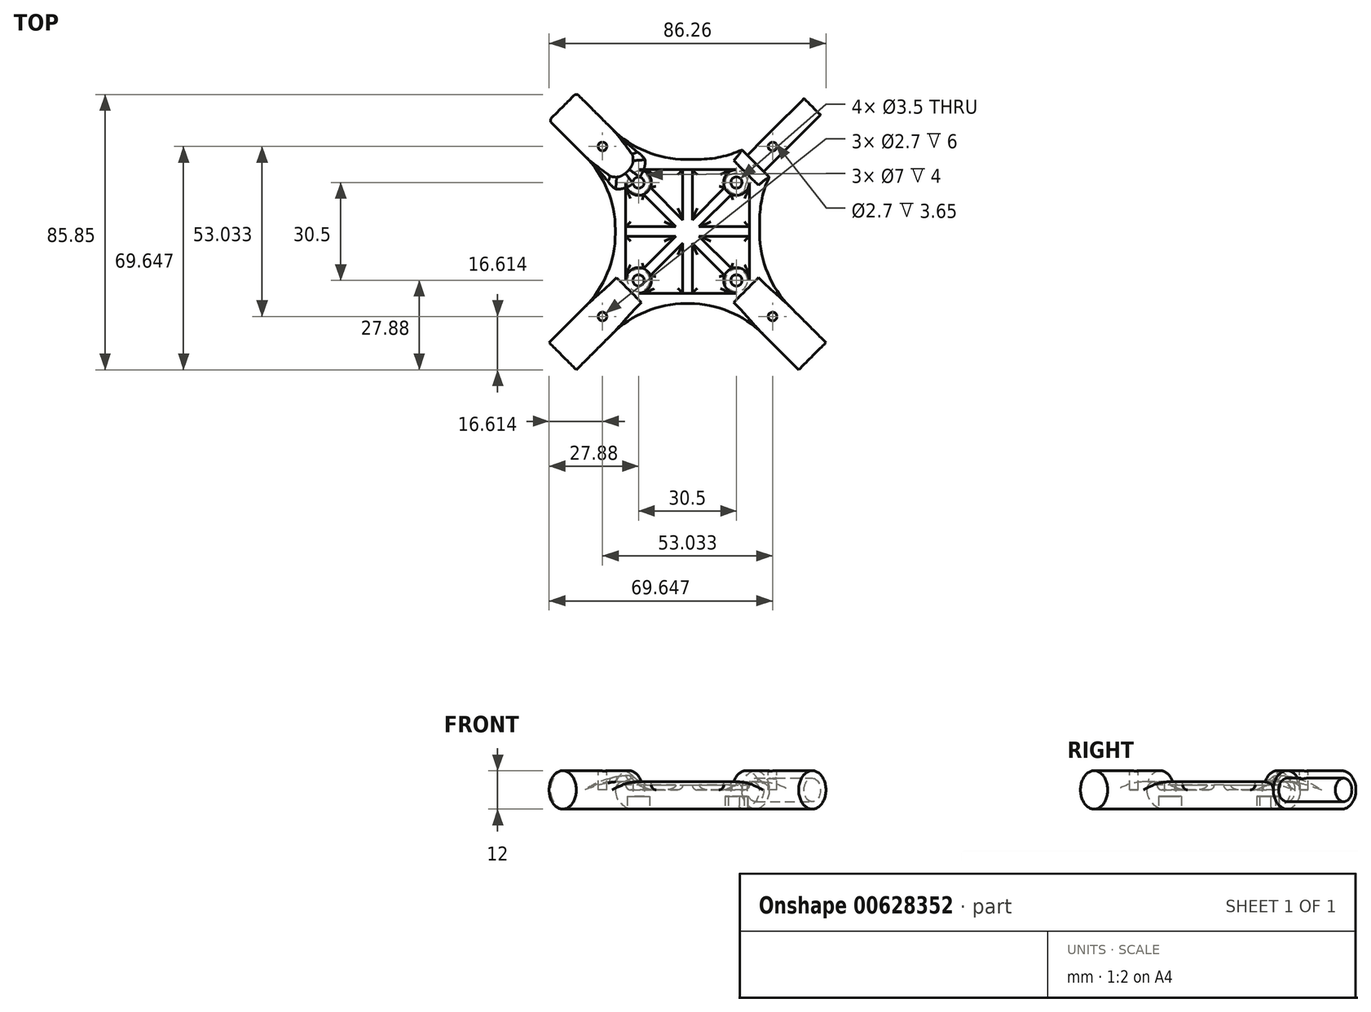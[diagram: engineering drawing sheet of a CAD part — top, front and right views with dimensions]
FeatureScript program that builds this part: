
annotation { "Feature Type Name" : "Feature", "Feature Type Description" : "" }
export const myFeature = defineFeature(function(context is Context, id is Id, definition is map)
    precondition{}
    {
        {
            var Q0;
            Q0=qCreatedBy(makeId("Top.planeOp"),FACE);
            var sketch = newSketch(context, id + "F0", { "sketchPlane" : qUnion([Q0])});
            skLineSegment(sketch, "E0.bottom", {"start": v(15.25, 15.25) * mm, "end": v(-15.25, 15.25) * mm});
            skLineSegment(sketch, "E0.top", {"start": v(15.25, -15.25) * mm, "end": v(-15.25, -15.25) * mm});
            skLineSegment(sketch, "E0.left", {"start": v(15.25, 15.25) * mm, "end": v(15.25, -15.25) * mm});
            skLineSegment(sketch, "E0.right", {"start": v(-15.25, 15.25) * mm, "end": v(-15.25, -15.25) * mm});
            skPoint(sketch, "E0.middle", {"position": v(0, 0) * mm});
            skCircle(sketch, "E1", {"center": v(-15.25, 15.25) * mm, "radius": 1.75 * mm});
            skCircle(sketch, "E2", {"center": v(15.25, 15.25) * mm, "radius": 1.75 * mm});
            skCircle(sketch, "E3", {"center": v(15.25, -15.25) * mm, "radius": 1.75 * mm});
            skCircle(sketch, "E4", {"center": v(-15.25, -15.25) * mm, "radius": 1.75 * mm});
            skLineSegment(sketch, "E5.bottom", {"start": v(22.5, 22.5) * mm, "end": v(-22.5, 22.5) * mm});
            skLineSegment(sketch, "E5.top", {"start": v(22.5, -22.5) * mm, "end": v(-22.5, -22.5) * mm});
            skLineSegment(sketch, "E5.left", {"start": v(22.5, 22.5) * mm, "end": v(22.5, -22.5) * mm});
            skLineSegment(sketch, "E5.right", {"start": v(-22.5, 22.5) * mm, "end": v(-22.5, -22.5) * mm});
            skSolve(sketch);
        }
        {
            var Q0;
            Q0=makeQuery(id+"F0.imprint","IMPRINT",FACE,{"disambiguationData":[TD([[makeQuery(id+"F0.imprint","IMPRINT",EDGE,{"derivedFrom":sQuery(id+"F0.wireOp",EDGE,"E5.bottom")}),1.0]])]});
            var Q1;
            {var subQ5=sQuery(id+"F0.wireOp",EDGE,"E2");var subQ13=sQuery(id+"F0.wireOp",EDGE,"E0.bottom");var subQ14=makeQuery(id+"F0.imprint","INTERSECT",VERTEX,{"derivedFrom":[subQ13,subQ5]});Q1=makeQuery(id+"F0.imprint","IMPRINT",FACE,{"disambiguationData":[TD([[makeQuery(id+"F0.imprint","IMPRINT",EDGE,{"disambiguationData":[TD([[subQ14,-1.0]])],"derivedFrom":subQ13}),1.0]])]});}
            extrude(context, id + "F1", {"entities" : qUnion([Q0, Q1]), "endBound" : BoundingType.SYMMETRIC, "depth" : 5 * mm, "offsetDistance" : 25 * mm});
        }
        {
            var Q0;
            Q0=makeQuery(id+"F1.opExtrude","CAP_FACE",FACE,{"disambiguationData":[OSD([sQuery(id+"F0.wireOp",EDGE,"E1"),sQuery(id+"F0.wireOp",EDGE,"E2"),sQuery(id+"F0.wireOp",EDGE,"E3"),sQuery(id+"F0.wireOp",EDGE,"E4"),sQuery(id+"F0.wireOp",EDGE,"E5.bottom"),sQuery(id+"F0.wireOp",EDGE,"E5.top"),sQuery(id+"F0.wireOp",EDGE,"E5.left"),sQuery(id+"F0.wireOp",EDGE,"E5.right")])],"isStart":false});
            var sketch = newSketch(context, id + "F2", { "sketchPlane" : qUnion([Q0])});
            skLineSegment(sketch, "E6", {"start": v(-22.5, 22.5) * mm, "end": v(0, 0) * mm});
            skLineSegment(sketch, "E7", {"start": v(0, 0) * mm, "end": v(22.5, 22.5) * mm});
            skLineSegment(sketch, "E8", {"start": v(22.5, -22.5) * mm, "end": v(0, 0) * mm});
            skLineSegment(sketch, "E9", {"start": v(-22.5, -22.5) * mm, "end": v(0, 0) * mm});
            skLineSegment(sketch, "E10", {"start": v(0, 0) * mm, "end": v(0, 22.5) * mm});
            skLineSegment(sketch, "E11", {"start": v(0, 0) * mm, "end": v(-22.5, 0) * mm});
            skLineSegment(sketch, "E12", {"start": v(0, 0) * mm, "end": v(22.5, 0) * mm});
            skLineSegment(sketch, "E13", {"start": v(0, 0) * mm, "end": v(0, -22.5) * mm});
            skCircle(sketch, "E14", {"center": v(-15.25, 15.25) * mm, "radius": 4 * mm});
            skCircle(sketch, "E15", {"center": v(15.25, 15.25) * mm, "radius": 4 * mm});
            skCircle(sketch, "E16", {"center": v(15.25, -15.25) * mm, "radius": 4 * mm});
            skCircle(sketch, "E17", {"center": v(-15.25, -15.25) * mm, "radius": 4 * mm});
            skLineSegment(sketch, "E18.0", {"start": v(15.25, 19.25) * mm, "end": v(-15.25, 19.25) * mm});
            skLineSegment(sketch, "E18.1", {"start": v(19.25, 15.25) * mm, "end": v(19.25, -15.25) * mm});
            skLineSegment(sketch, "E18.2", {"start": v(15.25, -19.25) * mm, "end": v(-15.25, -19.25) * mm});
            skLineSegment(sketch, "E18.3", {"start": v(-19.25, 15.25) * mm, "end": v(-19.25, -15.25) * mm});
            skLineSegment(sketch, "E19.0", {"start": v(1.5, 0) * mm, "end": v(1.5, 22.5) * mm});
            skLineSegment(sketch, "E19.1", {"start": v(1.5, 0) * mm, "end": v(1.5, -22.5) * mm});
            skLineSegment(sketch, "E20.0", {"start": v(-1.5, 0) * mm, "end": v(-1.5, 22.5) * mm});
            skLineSegment(sketch, "E20.1", {"start": v(-1.5, 0) * mm, "end": v(-1.5, -22.5) * mm});
            skLineSegment(sketch, "E21.0", {"start": v(0, 1.5) * mm, "end": v(-22.5, 1.5) * mm});
            skLineSegment(sketch, "E21.1", {"start": v(0, 1.5) * mm, "end": v(22.5, 1.5) * mm});
            skLineSegment(sketch, "E22.0", {"start": v(0, -1.5) * mm, "end": v(-22.5, -1.5) * mm});
            skLineSegment(sketch, "E22.1", {"start": v(0, -1.5) * mm, "end": v(22.5, -1.5) * mm});
            skLineSegment(sketch, "E23.0", {"start": v(21.44, -23.56) * mm, "end": v(-1.06, -1.06) * mm});
            skLineSegment(sketch, "E23.1", {"start": v(-23.56, 21.44) * mm, "end": v(-1.06, -1.06) * mm});
            skLineSegment(sketch, "E24.0", {"start": v(1.06, -1.06) * mm, "end": v(23.56, 21.44) * mm});
            skLineSegment(sketch, "E24.1", {"start": v(-21.44, -23.56) * mm, "end": v(1.06, -1.06) * mm});
            skLineSegment(sketch, "E25.0", {"start": v(-1.06, 1.06) * mm, "end": v(21.44, 23.56) * mm});
            skLineSegment(sketch, "E25.1", {"start": v(-23.56, -21.44) * mm, "end": v(-1.06, 1.06) * mm});
            skLineSegment(sketch, "E26.0", {"start": v(23.56, -21.44) * mm, "end": v(1.06, 1.06) * mm});
            skLineSegment(sketch, "E26.1", {"start": v(-21.44, 23.56) * mm, "end": v(1.06, 1.06) * mm});
            skSolve(sketch);
        }
        {
            var Q0;
            {var subQ0=sQuery(id+"F2.wireOp",EDGE,"E18.0");var subQ1=sQuery(id+"F2.wireOp",EDGE,"E15");var subQ2=makeQuery(id+"F2.imprint","INTERSECT",VERTEX,{"derivedFrom":[subQ1,subQ0]});Q0=makeQuery(id+"F2.imprint","IMPRINT",FACE,{"disambiguationData":[TD([[makeQuery(id+"F2.imprint","IMPRINT",EDGE,{"disambiguationData":[TD([[subQ2,-1.0]])],"derivedFrom":subQ1}),-1.0]])]});}
            var Q1;
            {var subQ0=sQuery(id+"F2.wireOp",EDGE,"E18.0");var subQ1=sQuery(id+"F2.wireOp",EDGE,"E14");var subQ2=makeQuery(id+"F2.imprint","INTERSECT",VERTEX,{"derivedFrom":[subQ1,subQ0]});Q1=makeQuery(id+"F2.imprint","IMPRINT",FACE,{"disambiguationData":[TD([[makeQuery(id+"F2.imprint","IMPRINT",EDGE,{"disambiguationData":[TD([[subQ2,1.0]])],"derivedFrom":subQ1}),-1.0]])]});}
            var Q2;
            {var subQ0=sQuery(id+"F2.wireOp",EDGE,"E18.3");var subQ1=sQuery(id+"F2.wireOp",EDGE,"E14");var subQ2=makeQuery(id+"F2.imprint","INTERSECT",VERTEX,{"derivedFrom":[subQ1,subQ0]});Q2=makeQuery(id+"F2.imprint","IMPRINT",FACE,{"disambiguationData":[TD([[makeQuery(id+"F2.imprint","IMPRINT",EDGE,{"disambiguationData":[TD([[subQ2,-1.0]])],"derivedFrom":subQ1}),-1.0]])]});}
            var Q3;
            {var subQ0=sQuery(id+"F2.wireOp",EDGE,"E18.3");var subQ1=sQuery(id+"F2.wireOp",EDGE,"E17");var subQ2=makeQuery(id+"F2.imprint","INTERSECT",VERTEX,{"derivedFrom":[subQ1,subQ0]});Q3=makeQuery(id+"F2.imprint","IMPRINT",FACE,{"disambiguationData":[TD([[makeQuery(id+"F2.imprint","IMPRINT",EDGE,{"disambiguationData":[TD([[subQ2,1.0]])],"derivedFrom":subQ1}),-1.0]])]});}
            var Q4;
            {var subQ0=sQuery(id+"F2.wireOp",EDGE,"E18.2");var subQ1=sQuery(id+"F2.wireOp",EDGE,"E17");var subQ2=makeQuery(id+"F2.imprint","INTERSECT",VERTEX,{"derivedFrom":[subQ1,subQ0]});Q4=makeQuery(id+"F2.imprint","IMPRINT",FACE,{"disambiguationData":[TD([[makeQuery(id+"F2.imprint","IMPRINT",EDGE,{"disambiguationData":[TD([[subQ2,-1.0]])],"derivedFrom":subQ1}),-1.0]])]});}
            var Q5;
            {var subQ0=sQuery(id+"F2.wireOp",EDGE,"E18.2");var subQ1=sQuery(id+"F2.wireOp",EDGE,"E16");var subQ2=makeQuery(id+"F2.imprint","INTERSECT",VERTEX,{"derivedFrom":[subQ1,subQ0]});Q5=makeQuery(id+"F2.imprint","IMPRINT",FACE,{"disambiguationData":[TD([[makeQuery(id+"F2.imprint","IMPRINT",EDGE,{"disambiguationData":[TD([[subQ2,1.0]])],"derivedFrom":subQ1}),-1.0]])]});}
            var Q6;
            {var subQ0=sQuery(id+"F2.wireOp",EDGE,"E18.1");var subQ1=sQuery(id+"F2.wireOp",EDGE,"E16");var subQ2=makeQuery(id+"F2.imprint","INTERSECT",VERTEX,{"derivedFrom":[subQ1,subQ0]});Q6=makeQuery(id+"F2.imprint","IMPRINT",FACE,{"disambiguationData":[TD([[makeQuery(id+"F2.imprint","IMPRINT",EDGE,{"disambiguationData":[TD([[subQ2,-1.0]])],"derivedFrom":subQ1}),-1.0]])]});}
            var Q7;
            {var subQ0=sQuery(id+"F2.wireOp",EDGE,"E18.1");var subQ1=sQuery(id+"F2.wireOp",EDGE,"E15");var subQ2=makeQuery(id+"F2.imprint","INTERSECT",VERTEX,{"derivedFrom":[subQ1,subQ0]});Q7=makeQuery(id+"F2.imprint","IMPRINT",FACE,{"disambiguationData":[TD([[makeQuery(id+"F2.imprint","IMPRINT",EDGE,{"disambiguationData":[TD([[subQ2,1.0]])],"derivedFrom":subQ1}),-1.0]])]});}
            extrude(context, id + "F3", {"entities" : qUnion([Q0, Q1, Q2, Q3, Q4, Q5, Q6, Q7]), "operationType" : NewBodyOperationType.REMOVE, "oppositeDirection" : true, "depth" : 2.5 * mm, "offsetDistance" : 25 * mm});
        }
        {
            var Q0;
            Q0=makeQuery(id+"F3.boolean.opBoolean","COPY",FACE,{"derivedFrom":makeQuery(id+"F3.opExtrude","CAP_FACE",FACE,{"disambiguationData":[OSD([sQuery(id+"F2.wireOp",EDGE,"E16"),sQuery(id+"F2.wireOp",EDGE,"E18.2"),sQuery(id+"F2.wireOp",EDGE,"E19.1"),sQuery(id+"F2.wireOp",EDGE,"E23.0")])],"isStart":false})});
            var Q1;
            Q1=makeQuery(id+"F3.boolean.opBoolean","COPY",FACE,{"derivedFrom":makeQuery(id+"F3.opExtrude","CAP_FACE",FACE,{"disambiguationData":[OSD([sQuery(id+"F2.wireOp",EDGE,"E17"),sQuery(id+"F2.wireOp",EDGE,"E18.2"),sQuery(id+"F2.wireOp",EDGE,"E20.1"),sQuery(id+"F2.wireOp",EDGE,"E24.1")])],"isStart":false})});
            var Q2;
            Q2=makeQuery(id+"F3.boolean.opBoolean","COPY",FACE,{"derivedFrom":makeQuery(id+"F3.opExtrude","CAP_FACE",FACE,{"disambiguationData":[OSD([sQuery(id+"F2.wireOp",EDGE,"E17"),sQuery(id+"F2.wireOp",EDGE,"E18.3"),sQuery(id+"F2.wireOp",EDGE,"E22.0"),sQuery(id+"F2.wireOp",EDGE,"E25.1")])],"isStart":false})});
            var Q3;
            Q3=makeQuery(id+"F3.boolean.opBoolean","COPY",FACE,{"derivedFrom":makeQuery(id+"F3.opExtrude","CAP_FACE",FACE,{"disambiguationData":[OSD([sQuery(id+"F2.wireOp",EDGE,"E14"),sQuery(id+"F2.wireOp",EDGE,"E18.3"),sQuery(id+"F2.wireOp",EDGE,"E21.0"),sQuery(id+"F2.wireOp",EDGE,"E23.1")])],"isStart":false})});
            var Q4;
            Q4=makeQuery(id+"F3.boolean.opBoolean","COPY",FACE,{"derivedFrom":makeQuery(id+"F3.opExtrude","CAP_FACE",FACE,{"disambiguationData":[OSD([sQuery(id+"F2.wireOp",EDGE,"E14"),sQuery(id+"F2.wireOp",EDGE,"E18.0"),sQuery(id+"F2.wireOp",EDGE,"E20.0"),sQuery(id+"F2.wireOp",EDGE,"E26.1")])],"isStart":false})});
            var Q5;
            Q5=makeQuery(id+"F3.boolean.opBoolean","COPY",FACE,{"derivedFrom":makeQuery(id+"F3.opExtrude","CAP_FACE",FACE,{"disambiguationData":[OSD([sQuery(id+"F2.wireOp",EDGE,"E15"),sQuery(id+"F2.wireOp",EDGE,"E18.0"),sQuery(id+"F2.wireOp",EDGE,"E19.0"),sQuery(id+"F2.wireOp",EDGE,"E25.0")])],"isStart":false})});
            var Q6;
            Q6=makeQuery(id+"F3.boolean.opBoolean","COPY",FACE,{"derivedFrom":makeQuery(id+"F3.opExtrude","CAP_FACE",FACE,{"disambiguationData":[OSD([sQuery(id+"F2.wireOp",EDGE,"E15"),sQuery(id+"F2.wireOp",EDGE,"E18.1"),sQuery(id+"F2.wireOp",EDGE,"E21.1"),sQuery(id+"F2.wireOp",EDGE,"E24.0")])],"isStart":false})});
            var Q7;
            Q7=makeQuery(id+"F3.boolean.opBoolean","COPY",FACE,{"derivedFrom":makeQuery(id+"F3.opExtrude","CAP_FACE",FACE,{"disambiguationData":[OSD([sQuery(id+"F2.wireOp",EDGE,"E16"),sQuery(id+"F2.wireOp",EDGE,"E18.1"),sQuery(id+"F2.wireOp",EDGE,"E22.1"),sQuery(id+"F2.wireOp",EDGE,"E26.0")])],"isStart":false})});
            fillet(context, id + "F4", {"entities" : qUnion([Q0, Q1, Q2, Q3, Q4, Q5, Q6, Q7]), "radius" : 1.5 * mm, "tangentPropagation" : true, "allowEdgeOverflow" : false});
        }
        {
            var Q0;
            Q0=qCreatedBy(makeId("Top.planeOp"),FACE);
            var sketch = newSketch(context, id + "F5", { "sketchPlane" : qUnion([Q0])});
            skLineSegment(sketch, "E27", {"start": v(0, 0) * mm, "end": v(-28.28, 28.28) * mm});
            skLineSegment(sketch, "E28", {"start": v(0, 0) * mm, "end": v(28.28, 28.28) * mm});
            skLineSegment(sketch, "E29", {"start": v(0, 0) * mm, "end": v(28.28, -28.28) * mm});
            skLineSegment(sketch, "E30", {"start": v(0, 0) * mm, "end": v(-28.28, -28.28) * mm});
            skLineSegment(sketch, "E31.0", {"start": v(4.24, -4.24) * mm, "end": v(32.53, 24.04) * mm});
            skLineSegment(sketch, "E31.1", {"start": v(4.24, -4.24) * mm, "end": v(-24.04, -32.53) * mm});
            skLineSegment(sketch, "E32.0", {"start": v(-4.24, 4.24) * mm, "end": v(-32.53, -24.04) * mm});
            skLineSegment(sketch, "E32.1", {"start": v(-4.24, 4.24) * mm, "end": v(24.04, 32.53) * mm});
            skLineSegment(sketch, "E33.0", {"start": v(-4.24, -4.24) * mm, "end": v(-32.53, 24.04) * mm});
            skLineSegment(sketch, "E33.1", {"start": v(-4.24, -4.24) * mm, "end": v(24.04, -32.53) * mm});
            skLineSegment(sketch, "E34.0", {"start": v(4.24, 4.24) * mm, "end": v(-24.04, 32.53) * mm});
            skLineSegment(sketch, "E34.1", {"start": v(4.24, 4.24) * mm, "end": v(32.53, -24.04) * mm});
            skLineSegment(sketch, "E35", {"start": v(24.04, -32.53) * mm, "end": v(32.53, -24.04) * mm});
            skLineSegment(sketch, "E36", {"start": v(-32.53, -24.04) * mm, "end": v(-24.04, -32.53) * mm});
            skLineSegment(sketch, "E37", {"start": v(24.04, 32.53) * mm, "end": v(32.53, 24.04) * mm});
            skLineSegment(sketch, "E38", {"start": v(-24.04, 32.53) * mm, "end": v(-32.53, 24.04) * mm});
            skLineSegment(sketch, "E39", {"start": v(22.5, 14.01) * mm, "end": v(14.01, 22.5) * mm});
            skLineSegment(sketch, "E40", {"start": v(22.5, -14.01) * mm, "end": v(14.01, -22.5) * mm});
            skLineSegment(sketch, "E41", {"start": v(-22.5, -14.01) * mm, "end": v(-14.01, -22.5) * mm});
            skLineSegment(sketch, "E42", {"start": v(-14.01, 22.5) * mm, "end": v(-22.5, 14.01) * mm});
            skSolve(sketch);
        }
        {
            var Q0;
            {var subQ0=sQuery(id+"F5.wireOp",EDGE,"E38");var subQ1=sQuery(id+"F5.wireOp",EDGE,"E27");var subQ2=makeQuery(id+"F5.imprint","INTERSECT",VERTEX,{"derivedFrom":[subQ1,subQ0]});Q0=makeQuery(id+"F5.imprint","IMPRINT",FACE,{"disambiguationData":[TD([[makeQuery(id+"F5.imprint","IMPRINT",EDGE,{"disambiguationData":[TD([[subQ2,1.0]])],"derivedFrom":subQ1}),-1.0]])]});}
            var Q1;
            {var subQ0=sQuery(id+"F5.wireOp",EDGE,"E38");var subQ1=sQuery(id+"F5.wireOp",EDGE,"E27");var subQ2=makeQuery(id+"F5.imprint","INTERSECT",VERTEX,{"derivedFrom":[subQ1,subQ0]});Q1=makeQuery(id+"F5.imprint","IMPRINT",FACE,{"disambiguationData":[TD([[makeQuery(id+"F5.imprint","IMPRINT",EDGE,{"disambiguationData":[TD([[subQ2,1.0]])],"derivedFrom":subQ1}),1.0]])]});}
            var Q2;
            {var subQ0=sQuery(id+"F5.wireOp",EDGE,"E36");var subQ1=sQuery(id+"F5.wireOp",EDGE,"E30");var subQ2=makeQuery(id+"F5.imprint","INTERSECT",VERTEX,{"derivedFrom":[subQ1,subQ0]});Q2=makeQuery(id+"F5.imprint","IMPRINT",FACE,{"disambiguationData":[TD([[makeQuery(id+"F5.imprint","IMPRINT",EDGE,{"disambiguationData":[TD([[subQ2,1.0]])],"derivedFrom":subQ1}),-1.0]])]});}
            var Q3;
            {var subQ0=sQuery(id+"F5.wireOp",EDGE,"E36");var subQ1=sQuery(id+"F5.wireOp",EDGE,"E30");var subQ2=makeQuery(id+"F5.imprint","INTERSECT",VERTEX,{"derivedFrom":[subQ1,subQ0]});Q3=makeQuery(id+"F5.imprint","IMPRINT",FACE,{"disambiguationData":[TD([[makeQuery(id+"F5.imprint","IMPRINT",EDGE,{"disambiguationData":[TD([[subQ2,1.0]])],"derivedFrom":subQ1}),1.0]])]});}
            var Q4;
            {var subQ0=sQuery(id+"F5.wireOp",EDGE,"E37");var subQ1=sQuery(id+"F5.wireOp",EDGE,"E28");var subQ2=makeQuery(id+"F5.imprint","INTERSECT",VERTEX,{"derivedFrom":[subQ1,subQ0]});Q4=makeQuery(id+"F5.imprint","IMPRINT",FACE,{"disambiguationData":[TD([[makeQuery(id+"F5.imprint","IMPRINT",EDGE,{"disambiguationData":[TD([[subQ2,1.0]])],"derivedFrom":subQ1}),1.0]])]});}
            var Q5;
            {var subQ0=sQuery(id+"F5.wireOp",EDGE,"E37");var subQ1=sQuery(id+"F5.wireOp",EDGE,"E28");var subQ2=makeQuery(id+"F5.imprint","INTERSECT",VERTEX,{"derivedFrom":[subQ1,subQ0]});Q5=makeQuery(id+"F5.imprint","IMPRINT",FACE,{"disambiguationData":[TD([[makeQuery(id+"F5.imprint","IMPRINT",EDGE,{"disambiguationData":[TD([[subQ2,1.0]])],"derivedFrom":subQ1}),-1.0]])]});}
            var Q6;
            {var subQ0=sQuery(id+"F5.wireOp",EDGE,"E35");var subQ1=sQuery(id+"F5.wireOp",EDGE,"E29");var subQ2=makeQuery(id+"F5.imprint","INTERSECT",VERTEX,{"derivedFrom":[subQ1,subQ0]});Q6=makeQuery(id+"F5.imprint","IMPRINT",FACE,{"disambiguationData":[TD([[makeQuery(id+"F5.imprint","IMPRINT",EDGE,{"disambiguationData":[TD([[subQ2,1.0]])],"derivedFrom":subQ1}),1.0]])]});}
            var Q7;
            {var subQ0=sQuery(id+"F5.wireOp",EDGE,"E35");var subQ1=sQuery(id+"F5.wireOp",EDGE,"E29");var subQ2=makeQuery(id+"F5.imprint","INTERSECT",VERTEX,{"derivedFrom":[subQ1,subQ0]});Q7=makeQuery(id+"F5.imprint","IMPRINT",FACE,{"disambiguationData":[TD([[makeQuery(id+"F5.imprint","IMPRINT",EDGE,{"disambiguationData":[TD([[subQ2,1.0]])],"derivedFrom":subQ1}),-1.0]])]});}
            extrude(context, id + "F6", {"entities" : qUnion([Q0, Q1, Q2, Q3, Q4, Q5, Q6, Q7]), "operationType" : NewBodyOperationType.ADD, "endBound" : BoundingType.SYMMETRIC, "depth" : 12 * mm, "offsetDistance" : 25 * mm});
        }
        {
            var Q0;
            Q0=makeQuery(id+"F6.opExtrude","SWEPT_FACE",FACE,{"disambiguationData":[OSD([sQuery(id+"F5.wireOp",EDGE,"E38")])]});
            extrude(context, id + "F7", {"entities" : qUnion([Q0]), "operationType" : NewBodyOperationType.ADD, "depth" : 15 * mm, "offsetDistance" : 25 * mm});
        }
        {
            var Q0;
            Q0=makeQuery(id+"F6.opExtrude","SWEPT_FACE",FACE,{"disambiguationData":[OSD([sQuery(id+"F5.wireOp",EDGE,"E36")])]});
            extrude(context, id + "F8", {"entities" : qUnion([Q0]), "operationType" : NewBodyOperationType.ADD, "depth" : 15 * mm, "offsetDistance" : 25 * mm});
        }
        {
            var Q0;
            Q0=makeQuery(id+"F6.opExtrude","SWEPT_FACE",FACE,{"disambiguationData":[OSD([sQuery(id+"F5.wireOp",EDGE,"E35")])]});
            extrude(context, id + "F9", {"entities" : qUnion([Q0]), "operationType" : NewBodyOperationType.ADD, "depth" : 15 * mm, "offsetDistance" : 25 * mm});
        }
        {
            var Q0;
            Q0=makeQuery(id+"F6.opExtrude","SWEPT_FACE",FACE,{"disambiguationData":[OSD([sQuery(id+"F5.wireOp",EDGE,"E37")])]});
            extrude(context, id + "F10", {"entities" : qUnion([Q0]), "operationType" : NewBodyOperationType.ADD, "depth" : 15 * mm, "offsetDistance" : 25 * mm});
        }
        {
            var Q0;
            Q0=makeQuery(id+"F10.opExtrude","CAP_FACE",FACE,{"disambiguationData":[OSD([sQuery(id+"F5.wireOp",EDGE,"E37")])],"isStart":false});
            var sketch = newSketch(context, id + "F11", { "sketchPlane" : qUnion([Q0])});
            skLineSegment(sketch, "E43", {"start": v(6, 6) * mm, "end": v(-6, -6) * mm});
            skCircle(sketch, "E44", {"center": v(0, 0) * mm, "radius": 3.65 * mm});
            skSolve(sketch);
        }
        {
            var Q0;
            {var subQ0=sQuery(id+"F11.wireOp",EDGE,"E44");var subQ1=sQuery(id+"F11.wireOp",EDGE,"E43");var subQ2=makeQuery(id+"F11.imprint","INTERSECT",VERTEX,{"disambiguationData":[OD(0.0)],"derivedFrom":[subQ1,subQ0]});Q0=makeQuery(id+"F11.imprint","IMPRINT",FACE,{"disambiguationData":[TD([[makeQuery(id+"F11.imprint","IMPRINT",EDGE,{"disambiguationData":[TD([[subQ2,-1.0]])],"derivedFrom":subQ1}),-1.0]])]});}
            var Q1;
            {var subQ0=sQuery(id+"F11.wireOp",EDGE,"E44");var subQ1=sQuery(id+"F11.wireOp",EDGE,"E43");var subQ2=makeQuery(id+"F11.imprint","INTERSECT",VERTEX,{"disambiguationData":[OD(0.0)],"derivedFrom":[subQ1,subQ0]});Q1=makeQuery(id+"F11.imprint","IMPRINT",FACE,{"disambiguationData":[TD([[makeQuery(id+"F11.imprint","IMPRINT",EDGE,{"disambiguationData":[TD([[subQ2,-1.0]])],"derivedFrom":subQ1}),1.0]])]});}
            extrude(context, id + "F12", {"entities" : qUnion([Q0, Q1]), "operationType" : NewBodyOperationType.REMOVE, "oppositeDirection" : true, "depth" : 25 * mm, "offsetDistance" : 25 * mm});
        }
        {
            var Q0;
            Q0=qCreatedBy(makeId("Right.planeOp"),FACE);
            var sketch = newSketch(context, id + "F13", { "sketchPlane" : qUnion([Q0])});
            skLineSegment(sketch, "E45", {"start": v(0, 0) * mm, "end": v(0, 67.2) * mm});
            skSolve(sketch);
        }
        {
            var Q0;
            {var subQ0=sQuery(id+"F5.wireOp",EDGE,"E37");Q0=makeQuery(id+"F10.boolean.opBoolean","MERGE",FACE,{"derivedFrom":[makeQuery(id+"F6.opExtrude","CAP_FACE",FACE,{"disambiguationData":[OSD([sQuery(id+"F5.wireOp",EDGE,"E31.0"),sQuery(id+"F5.wireOp",EDGE,"E32.1"),subQ0,sQuery(id+"F5.wireOp",EDGE,"E39")])],"isStart":false}),makeQuery(id+"F10.opExtrude","SWEPT_FACE",FACE,{"disambiguationData":[OSD([subQ0]),TDD([makeQuery(id+"F6.opExtrude","CAP_EDGE",EDGE,{"disambiguationData":[OSD([subQ0])],"isStart":false})])]})]});}
            var sketch = newSketch(context, id + "F14", { "sketchPlane" : qUnion([Q0])});
            skCircle(sketch, "E46", {"center": v(26.52, 26.52) * mm, "radius": 1.35 * mm});
            skCircle(sketch, "E47", {"center": v(-26.52, 26.52) * mm, "radius": 1.35 * mm});
            skCircle(sketch, "E48", {"center": v(-26.52, -26.52) * mm, "radius": 1.35 * mm});
            skCircle(sketch, "E49", {"center": v(26.52, -26.52) * mm, "radius": 1.35 * mm});
            skCircle(sketch, "E50", {"center": v(0, 0) * mm, "radius": 37.5 * mm});
            skSolve(sketch);
        }
        {
            var Q0;
            {var subQ0=sQuery(id+"F14.wireOp",EDGE,"E46");var subQ1=sQuery(id+"F5.wireOp",EDGE,"E37");var subQ2=makeQuery(id+"F6.opExtrude","CAP_EDGE",EDGE,{"disambiguationData":[OSD([subQ1])],"isStart":false});var subQ3=makeQuery(id+"F10.boolean.opBoolean","MERGE",FACE,{"derivedFrom":[makeQuery(id+"F6.opExtrude","CAP_FACE",FACE,{"disambiguationData":[OSD([sQuery(id+"F5.wireOp",EDGE,"E31.0"),sQuery(id+"F5.wireOp",EDGE,"E32.1"),subQ1,sQuery(id+"F5.wireOp",EDGE,"E39")])],"isStart":false}),makeQuery(id+"F10.opExtrude","SWEPT_FACE",FACE,{"disambiguationData":[OSD([subQ1]),TDD([subQ2])]})]});var subQ4=makeQuery(id+"F1Ntn1prAlgGOFy_1.opFillet","BLEND_EDGE",EDGE,{"blendedFrom":[makeQuery(id+"FOx5YZa0fqgjj0m_1.opChamfer","BLEND_EDGE",EDGE,{"blendedFrom":[makeQuery(id+"F10.opExtrude","CAP_EDGE",EDGE,{"disambiguationData":[OSD([subQ1]),TDD([subQ2])],"isStart":false}),subQ3],"blendedInto":[subQ3]}),subQ3],"blendedInto":[subQ3]});var subQ5=makeQuery(id+"F14.imprint","INTERSECT",VERTEX,{"disambiguationData":[OD(0.0)],"derivedFrom":[subQ4,subQ0]});Q0=makeQuery(id+"F14.imprint","IMPRINT",FACE,{"disambiguationData":[TD([[makeQuery(id+"F14.imprint","IMPRINT",EDGE,{"disambiguationData":[TD([[subQ5,1.0]])],"derivedFrom":subQ0}),1.0]])]});}
            var Q1;
            {var subQ0=sQuery(id+"F14.wireOp",EDGE,"E46");var subQ1=sQuery(id+"F5.wireOp",EDGE,"E37");var subQ2=makeQuery(id+"F6.opExtrude","CAP_EDGE",EDGE,{"disambiguationData":[OSD([subQ1])],"isStart":false});var subQ3=makeQuery(id+"F10.boolean.opBoolean","MERGE",FACE,{"derivedFrom":[makeQuery(id+"F6.opExtrude","CAP_FACE",FACE,{"disambiguationData":[OSD([sQuery(id+"F5.wireOp",EDGE,"E31.0"),sQuery(id+"F5.wireOp",EDGE,"E32.1"),subQ1,sQuery(id+"F5.wireOp",EDGE,"E39")])],"isStart":false}),makeQuery(id+"F10.opExtrude","SWEPT_FACE",FACE,{"disambiguationData":[OSD([subQ1]),TDD([subQ2])]})]});var subQ4=makeQuery(id+"F1Ntn1prAlgGOFy_1.opFillet","BLEND_EDGE",EDGE,{"blendedFrom":[makeQuery(id+"FOx5YZa0fqgjj0m_1.opChamfer","BLEND_EDGE",EDGE,{"blendedFrom":[makeQuery(id+"F10.opExtrude","CAP_EDGE",EDGE,{"disambiguationData":[OSD([subQ1]),TDD([subQ2])],"isStart":false}),subQ3],"blendedInto":[subQ3]}),subQ3],"blendedInto":[subQ3]});var subQ5=makeQuery(id+"F14.imprint","INTERSECT",VERTEX,{"disambiguationData":[OD(0.0)],"derivedFrom":[subQ4,subQ0]});Q1=makeQuery(id+"F14.imprint","IMPRINT",FACE,{"disambiguationData":[TD([[makeQuery(id+"F14.imprint","IMPRINT",EDGE,{"disambiguationData":[TD([[subQ5,-1.0]])],"derivedFrom":subQ0}),1.0]])]});}
            var Q2;
            Q2=makeQuery(id+"F14.imprint","IMPRINT",FACE,{"disambiguationData":[TD([[makeQuery(id+"F14.imprint","IMPRINT",EDGE,{"derivedFrom":sQuery(id+"F14.wireOp",EDGE,"E49")}),1.0]])]});
            var Q3;
            Q3=makeQuery(id+"F14.imprint","IMPRINT",FACE,{"disambiguationData":[TD([[makeQuery(id+"F14.imprint","IMPRINT",EDGE,{"derivedFrom":sQuery(id+"F14.wireOp",EDGE,"E47")}),1.0]])]});
            var Q4;
            Q4=makeQuery(id+"F14.imprint","IMPRINT",FACE,{"disambiguationData":[TD([[makeQuery(id+"F14.imprint","IMPRINT",EDGE,{"derivedFrom":sQuery(id+"F14.wireOp",EDGE,"E48")}),1.0]])]});
            var Q5;
            Q5=makeQuery(id+"F12.boolean.opBoolean","COPY",FACE,{"derivedFrom":makeQuery(id+"F12.opExtrude","SWEPT_FACE",FACE,{"disambiguationData":[OSD([sQuery(id+"F11.wireOp",EDGE,"E44")])]})});
            extrude(context, id + "F15", {"entities" : qUnion([Q0, Q1, Q2, Q3, Q4]), "operationType" : NewBodyOperationType.REMOVE, "oppositeDirection" : true, "depth" : 6 * mm, "endBoundEntityFace" : qUnion([Q5]), "offsetDistance" : 25 * mm});
        }
        {
            var Q0;
            Q0=makeQuery(id+"F1.opExtrude","CAP_FACE",FACE,{"disambiguationData":[OSD([sQuery(id+"F0.wireOp",EDGE,"E1"),sQuery(id+"F0.wireOp",EDGE,"E2"),sQuery(id+"F0.wireOp",EDGE,"E3"),sQuery(id+"F0.wireOp",EDGE,"E4"),sQuery(id+"F0.wireOp",EDGE,"E5.bottom"),sQuery(id+"F0.wireOp",EDGE,"E5.top"),sQuery(id+"F0.wireOp",EDGE,"E5.left"),sQuery(id+"F0.wireOp",EDGE,"E5.right")])],"isStart":true});
            var Q1;
            {var subQ0=sQuery(id+"F5.wireOp",EDGE,"E37");Q1=makeQuery(id+"F10.boolean.opBoolean","MERGE",FACE,{"derivedFrom":[makeQuery(id+"F6.opExtrude","CAP_FACE",FACE,{"disambiguationData":[OSD([sQuery(id+"F5.wireOp",EDGE,"E31.0"),sQuery(id+"F5.wireOp",EDGE,"E32.1"),subQ0,sQuery(id+"F5.wireOp",EDGE,"E39")])],"isStart":true}),makeQuery(id+"F10.opExtrude","SWEPT_FACE",FACE,{"disambiguationData":[OSD([subQ0]),TDD([makeQuery(id+"F6.opExtrude","CAP_EDGE",EDGE,{"disambiguationData":[OSD([subQ0])],"isStart":true})])]})]});}
            extrude(context, id + "F16", {"entities" : qUnion([Q0]), "operationType" : NewBodyOperationType.ADD, "endBound" : BoundingType.UP_TO_SURFACE, "depth" : 3.4 * mm, "endBoundEntityFace" : qUnion([Q1]), "offsetDistance" : 25 * mm});
        }
        {
            var Q0;
            {var subQ0=sQuery(id+"F5.wireOp",EDGE,"E41");var subQ1=makeQuery(id+"F6.opExtrude","SWEPT_FACE",FACE,{"disambiguationData":[OSD([subQ0])]});var subQ2=sQuery(id+"F0.wireOp",EDGE,"E5.right");var subQ3=sQuery(id+"F0.wireOp",EDGE,"E5.left");var subQ4=sQuery(id+"F0.wireOp",EDGE,"E5.top");var subQ5=sQuery(id+"F0.wireOp",EDGE,"E5.bottom");var subQ6=sQuery(id+"F0.wireOp",EDGE,"E4");var subQ7=sQuery(id+"F0.wireOp",EDGE,"E3");var subQ8=sQuery(id+"F0.wireOp",EDGE,"E2");var subQ9=sQuery(id+"F0.wireOp",EDGE,"E1");var subQ10=makeQuery(id+"F1.opExtrude","CAP_FACE",FACE,{"disambiguationData":[OSD([subQ9,subQ8,subQ7,subQ6,subQ5,subQ4,subQ3,subQ2])],"isStart":true});var subQ11=makeQuery(id+"F1.opExtrude","SWEPT_FACE",FACE,{"disambiguationData":[OSD([subQ4])]});var subQ12=sQuery(id+"F5.wireOp",EDGE,"E31.1");var subQ13=makeQuery(id+"F6.opExtrude","SWEPT_FACE",FACE,{"disambiguationData":[OSD([subQ12])]});var subQ14=makeQuery(id+"F6.opExtrude","SWEPT_EDGE",EDGE,{"disambiguationData":[OSD([subQ12,subQ0])]});Q0=makeQuery(id+"F16.boolean.opBoolean","MERGE",EDGE,{"derivedFrom":[makeQuery(id+"F6.boolean.opBoolean","SPLIT",EDGE,{"disambiguationData":[topologyDisambiguationEdgeConnected([subQ13,subQ1]),TD([makeQuery(id+"F6.opExtrude","CAP_FACE",FACE,{"disambiguationData":[OSD([subQ12,sQuery(id+"F5.wireOp",EDGE,"E32.0"),sQuery(id+"F5.wireOp",EDGE,"E36"),subQ0])],"isStart":true})])],"derivedFrom":subQ14}),makeQuery(id+"F6.boolean.opBoolean","SPLIT",EDGE,{"disambiguationData":[topologyDisambiguationEdgeConnected([subQ11,subQ13])],"derivedFrom":subQ14}),makeQuery(id+"F16.opExtrude","SWEPT_EDGE",EDGE,{"disambiguationData":[OSD([subQ9,subQ8,subQ7,subQ6,subQ5,subQ4,subQ3,subQ2,subQ0]),TDD([makeQuery(id+"F6.boolean.opBoolean","INTERSECT",VERTEX,{"disambiguationData":[OD(0.0)],"derivedFrom":[subQ10,subQ1]})])]})]});}
            var Q1;
            {var subQ0=sQuery(id+"F5.wireOp",EDGE,"E40");var subQ1=makeQuery(id+"F6.opExtrude","SWEPT_FACE",FACE,{"disambiguationData":[OSD([subQ0])]});var subQ2=sQuery(id+"F0.wireOp",EDGE,"E5.right");var subQ3=sQuery(id+"F0.wireOp",EDGE,"E5.left");var subQ4=sQuery(id+"F0.wireOp",EDGE,"E5.top");var subQ5=sQuery(id+"F0.wireOp",EDGE,"E5.bottom");var subQ6=sQuery(id+"F0.wireOp",EDGE,"E4");var subQ7=sQuery(id+"F0.wireOp",EDGE,"E3");var subQ8=sQuery(id+"F0.wireOp",EDGE,"E2");var subQ9=sQuery(id+"F0.wireOp",EDGE,"E1");var subQ10=makeQuery(id+"F1.opExtrude","CAP_FACE",FACE,{"disambiguationData":[OSD([subQ9,subQ8,subQ7,subQ6,subQ5,subQ4,subQ3,subQ2])],"isStart":true});var subQ11=makeQuery(id+"F1.opExtrude","SWEPT_FACE",FACE,{"disambiguationData":[OSD([subQ4])]});var subQ12=sQuery(id+"F5.wireOp",EDGE,"E33.1");var subQ13=makeQuery(id+"F6.opExtrude","SWEPT_FACE",FACE,{"disambiguationData":[OSD([subQ12])]});var subQ14=makeQuery(id+"F6.opExtrude","SWEPT_EDGE",EDGE,{"disambiguationData":[OSD([subQ12,subQ0])]});Q1=makeQuery(id+"F16.boolean.opBoolean","MERGE",EDGE,{"derivedFrom":[makeQuery(id+"F6.boolean.opBoolean","SPLIT",EDGE,{"disambiguationData":[topologyDisambiguationEdgeConnected([subQ13,subQ1]),TD([makeQuery(id+"F6.opExtrude","CAP_FACE",FACE,{"disambiguationData":[OSD([subQ12,sQuery(id+"F5.wireOp",EDGE,"E34.1"),sQuery(id+"F5.wireOp",EDGE,"E35"),subQ0])],"isStart":true})])],"derivedFrom":subQ14}),makeQuery(id+"F6.boolean.opBoolean","SPLIT",EDGE,{"disambiguationData":[topologyDisambiguationEdgeConnected([subQ11,subQ13])],"derivedFrom":subQ14}),makeQuery(id+"F16.opExtrude","SWEPT_EDGE",EDGE,{"disambiguationData":[OSD([subQ9,subQ8,subQ7,subQ6,subQ5,subQ4,subQ3,subQ2,subQ0]),TDD([makeQuery(id+"F6.boolean.opBoolean","INTERSECT",VERTEX,{"disambiguationData":[OD(0.0)],"derivedFrom":[subQ10,subQ1]})])]})]});}
            var Q2;
            {var subQ0=sQuery(id+"F5.wireOp",EDGE,"E40");var subQ1=makeQuery(id+"F6.opExtrude","SWEPT_FACE",FACE,{"disambiguationData":[OSD([subQ0])]});var subQ2=sQuery(id+"F0.wireOp",EDGE,"E5.right");var subQ3=sQuery(id+"F0.wireOp",EDGE,"E5.left");var subQ4=sQuery(id+"F0.wireOp",EDGE,"E5.top");var subQ5=sQuery(id+"F0.wireOp",EDGE,"E5.bottom");var subQ6=sQuery(id+"F0.wireOp",EDGE,"E4");var subQ7=sQuery(id+"F0.wireOp",EDGE,"E3");var subQ8=sQuery(id+"F0.wireOp",EDGE,"E2");var subQ9=sQuery(id+"F0.wireOp",EDGE,"E1");var subQ10=makeQuery(id+"F1.opExtrude","CAP_FACE",FACE,{"disambiguationData":[OSD([subQ9,subQ8,subQ7,subQ6,subQ5,subQ4,subQ3,subQ2])],"isStart":true});var subQ11=makeQuery(id+"F1.opExtrude","SWEPT_FACE",FACE,{"disambiguationData":[OSD([subQ3])]});var subQ12=sQuery(id+"F5.wireOp",EDGE,"E34.1");var subQ13=makeQuery(id+"F6.opExtrude","SWEPT_FACE",FACE,{"disambiguationData":[OSD([subQ12])]});var subQ14=makeQuery(id+"F6.opExtrude","SWEPT_EDGE",EDGE,{"disambiguationData":[OSD([subQ12,subQ0])]});Q2=makeQuery(id+"F16.boolean.opBoolean","MERGE",EDGE,{"derivedFrom":[makeQuery(id+"F6.boolean.opBoolean","SPLIT",EDGE,{"disambiguationData":[topologyDisambiguationEdgeConnected([subQ13,subQ1]),TD([makeQuery(id+"F6.opExtrude","CAP_FACE",FACE,{"disambiguationData":[OSD([sQuery(id+"F5.wireOp",EDGE,"E33.1"),subQ12,sQuery(id+"F5.wireOp",EDGE,"E35"),subQ0])],"isStart":true})])],"derivedFrom":subQ14}),makeQuery(id+"F6.boolean.opBoolean","SPLIT",EDGE,{"disambiguationData":[topologyDisambiguationEdgeConnected([subQ11,subQ13])],"derivedFrom":subQ14}),makeQuery(id+"F16.opExtrude","SWEPT_EDGE",EDGE,{"disambiguationData":[OSD([subQ9,subQ8,subQ7,subQ6,subQ5,subQ4,subQ3,subQ2,subQ0]),TDD([makeQuery(id+"F6.boolean.opBoolean","INTERSECT",VERTEX,{"disambiguationData":[OD(1.0)],"derivedFrom":[subQ10,subQ1]})])]})]});}
            var Q3;
            {var subQ0=sQuery(id+"F5.wireOp",EDGE,"E39");var subQ1=makeQuery(id+"F6.opExtrude","SWEPT_FACE",FACE,{"disambiguationData":[OSD([subQ0])]});var subQ2=sQuery(id+"F0.wireOp",EDGE,"E5.right");var subQ3=sQuery(id+"F0.wireOp",EDGE,"E5.left");var subQ4=sQuery(id+"F0.wireOp",EDGE,"E5.top");var subQ5=sQuery(id+"F0.wireOp",EDGE,"E5.bottom");var subQ6=sQuery(id+"F0.wireOp",EDGE,"E4");var subQ7=sQuery(id+"F0.wireOp",EDGE,"E3");var subQ8=sQuery(id+"F0.wireOp",EDGE,"E2");var subQ9=sQuery(id+"F0.wireOp",EDGE,"E1");var subQ10=makeQuery(id+"F1.opExtrude","CAP_FACE",FACE,{"disambiguationData":[OSD([subQ9,subQ8,subQ7,subQ6,subQ5,subQ4,subQ3,subQ2])],"isStart":true});var subQ11=makeQuery(id+"F1.opExtrude","SWEPT_FACE",FACE,{"disambiguationData":[OSD([subQ3])]});var subQ12=sQuery(id+"F5.wireOp",EDGE,"E31.0");var subQ13=makeQuery(id+"F6.opExtrude","SWEPT_FACE",FACE,{"disambiguationData":[OSD([subQ12])]});var subQ14=makeQuery(id+"F6.opExtrude","SWEPT_EDGE",EDGE,{"disambiguationData":[OSD([subQ12,subQ0])]});Q3=makeQuery(id+"F16.boolean.opBoolean","MERGE",EDGE,{"derivedFrom":[makeQuery(id+"F6.boolean.opBoolean","SPLIT",EDGE,{"disambiguationData":[topologyDisambiguationEdgeConnected([subQ13,subQ1]),TD([makeQuery(id+"F6.opExtrude","CAP_FACE",FACE,{"disambiguationData":[OSD([subQ12,sQuery(id+"F5.wireOp",EDGE,"E32.1"),sQuery(id+"F5.wireOp",EDGE,"E37"),subQ0])],"isStart":true})])],"derivedFrom":subQ14}),makeQuery(id+"F6.boolean.opBoolean","SPLIT",EDGE,{"disambiguationData":[topologyDisambiguationEdgeConnected([subQ11,subQ13])],"derivedFrom":subQ14}),makeQuery(id+"F16.opExtrude","SWEPT_EDGE",EDGE,{"disambiguationData":[OSD([subQ9,subQ8,subQ7,subQ6,subQ5,subQ4,subQ3,subQ2,subQ0]),TDD([makeQuery(id+"F6.boolean.opBoolean","INTERSECT",VERTEX,{"disambiguationData":[OD(1.0)],"derivedFrom":[subQ10,subQ1]})])]})]});}
            var Q4;
            {var subQ0=sQuery(id+"F5.wireOp",EDGE,"E39");var subQ1=makeQuery(id+"F6.opExtrude","SWEPT_FACE",FACE,{"disambiguationData":[OSD([subQ0])]});var subQ2=sQuery(id+"F0.wireOp",EDGE,"E5.right");var subQ3=sQuery(id+"F0.wireOp",EDGE,"E5.left");var subQ4=sQuery(id+"F0.wireOp",EDGE,"E5.top");var subQ5=sQuery(id+"F0.wireOp",EDGE,"E5.bottom");var subQ6=sQuery(id+"F0.wireOp",EDGE,"E4");var subQ7=sQuery(id+"F0.wireOp",EDGE,"E3");var subQ8=sQuery(id+"F0.wireOp",EDGE,"E2");var subQ9=sQuery(id+"F0.wireOp",EDGE,"E1");var subQ10=makeQuery(id+"F1.opExtrude","CAP_FACE",FACE,{"disambiguationData":[OSD([subQ9,subQ8,subQ7,subQ6,subQ5,subQ4,subQ3,subQ2])],"isStart":true});var subQ11=makeQuery(id+"F1.opExtrude","SWEPT_FACE",FACE,{"disambiguationData":[OSD([subQ5])]});var subQ12=sQuery(id+"F5.wireOp",EDGE,"E32.1");var subQ13=makeQuery(id+"F6.opExtrude","SWEPT_FACE",FACE,{"disambiguationData":[OSD([subQ12])]});var subQ14=makeQuery(id+"F6.opExtrude","SWEPT_EDGE",EDGE,{"disambiguationData":[OSD([subQ12,subQ0])]});Q4=makeQuery(id+"F16.boolean.opBoolean","MERGE",EDGE,{"derivedFrom":[makeQuery(id+"F6.boolean.opBoolean","SPLIT",EDGE,{"disambiguationData":[topologyDisambiguationEdgeConnected([subQ13,subQ1]),TD([makeQuery(id+"F6.opExtrude","CAP_FACE",FACE,{"disambiguationData":[OSD([sQuery(id+"F5.wireOp",EDGE,"E31.0"),subQ12,sQuery(id+"F5.wireOp",EDGE,"E37"),subQ0])],"isStart":true})])],"derivedFrom":subQ14}),makeQuery(id+"F6.boolean.opBoolean","SPLIT",EDGE,{"disambiguationData":[topologyDisambiguationEdgeConnected([subQ11,subQ13])],"derivedFrom":subQ14}),makeQuery(id+"F16.opExtrude","SWEPT_EDGE",EDGE,{"disambiguationData":[OSD([subQ9,subQ8,subQ7,subQ6,subQ5,subQ4,subQ3,subQ2,subQ0]),TDD([makeQuery(id+"F6.boolean.opBoolean","INTERSECT",VERTEX,{"disambiguationData":[OD(0.0)],"derivedFrom":[subQ10,subQ1]})])]})]});}
            var Q5;
            {var subQ0=sQuery(id+"F5.wireOp",EDGE,"E42");var subQ1=makeQuery(id+"F6.opExtrude","SWEPT_FACE",FACE,{"disambiguationData":[OSD([subQ0])]});var subQ2=sQuery(id+"F0.wireOp",EDGE,"E5.right");var subQ3=sQuery(id+"F0.wireOp",EDGE,"E5.left");var subQ4=sQuery(id+"F0.wireOp",EDGE,"E5.top");var subQ5=sQuery(id+"F0.wireOp",EDGE,"E5.bottom");var subQ6=sQuery(id+"F0.wireOp",EDGE,"E4");var subQ7=sQuery(id+"F0.wireOp",EDGE,"E3");var subQ8=sQuery(id+"F0.wireOp",EDGE,"E2");var subQ9=sQuery(id+"F0.wireOp",EDGE,"E1");var subQ10=makeQuery(id+"F1.opExtrude","CAP_FACE",FACE,{"disambiguationData":[OSD([subQ9,subQ8,subQ7,subQ6,subQ5,subQ4,subQ3,subQ2])],"isStart":true});var subQ11=makeQuery(id+"F1.opExtrude","SWEPT_FACE",FACE,{"disambiguationData":[OSD([subQ5])]});var subQ12=sQuery(id+"F5.wireOp",EDGE,"E34.0");var subQ13=makeQuery(id+"F6.opExtrude","SWEPT_FACE",FACE,{"disambiguationData":[OSD([subQ12])]});var subQ14=makeQuery(id+"F6.opExtrude","SWEPT_EDGE",EDGE,{"disambiguationData":[OSD([subQ12,subQ0])]});Q5=makeQuery(id+"F16.boolean.opBoolean","MERGE",EDGE,{"derivedFrom":[makeQuery(id+"F6.boolean.opBoolean","SPLIT",EDGE,{"disambiguationData":[topologyDisambiguationEdgeConnected([subQ13,subQ1]),TD([makeQuery(id+"F6.opExtrude","CAP_FACE",FACE,{"disambiguationData":[OSD([sQuery(id+"F5.wireOp",EDGE,"E33.0"),subQ12,sQuery(id+"F5.wireOp",EDGE,"E38"),subQ0])],"isStart":true})])],"derivedFrom":subQ14}),makeQuery(id+"F6.boolean.opBoolean","SPLIT",EDGE,{"disambiguationData":[topologyDisambiguationEdgeConnected([subQ11,subQ13])],"derivedFrom":subQ14}),makeQuery(id+"F16.opExtrude","SWEPT_EDGE",EDGE,{"disambiguationData":[OSD([subQ9,subQ8,subQ7,subQ6,subQ5,subQ4,subQ3,subQ2,subQ0]),TDD([makeQuery(id+"F6.boolean.opBoolean","INTERSECT",VERTEX,{"disambiguationData":[OD(0.0)],"derivedFrom":[subQ10,subQ1]})])]})]});}
            var Q6;
            {var subQ0=sQuery(id+"F5.wireOp",EDGE,"E42");var subQ1=makeQuery(id+"F6.opExtrude","SWEPT_FACE",FACE,{"disambiguationData":[OSD([subQ0])]});var subQ2=sQuery(id+"F0.wireOp",EDGE,"E5.right");var subQ3=sQuery(id+"F0.wireOp",EDGE,"E5.left");var subQ4=sQuery(id+"F0.wireOp",EDGE,"E5.top");var subQ5=sQuery(id+"F0.wireOp",EDGE,"E5.bottom");var subQ6=sQuery(id+"F0.wireOp",EDGE,"E4");var subQ7=sQuery(id+"F0.wireOp",EDGE,"E3");var subQ8=sQuery(id+"F0.wireOp",EDGE,"E2");var subQ9=sQuery(id+"F0.wireOp",EDGE,"E1");var subQ10=makeQuery(id+"F1.opExtrude","CAP_FACE",FACE,{"disambiguationData":[OSD([subQ9,subQ8,subQ7,subQ6,subQ5,subQ4,subQ3,subQ2])],"isStart":true});var subQ11=makeQuery(id+"F1.opExtrude","SWEPT_FACE",FACE,{"disambiguationData":[OSD([subQ2])]});var subQ12=sQuery(id+"F5.wireOp",EDGE,"E33.0");var subQ13=makeQuery(id+"F6.opExtrude","SWEPT_FACE",FACE,{"disambiguationData":[OSD([subQ12])]});var subQ14=makeQuery(id+"F6.opExtrude","SWEPT_EDGE",EDGE,{"disambiguationData":[OSD([subQ12,subQ0])]});Q6=makeQuery(id+"F16.boolean.opBoolean","MERGE",EDGE,{"derivedFrom":[makeQuery(id+"F6.boolean.opBoolean","SPLIT",EDGE,{"disambiguationData":[topologyDisambiguationEdgeConnected([subQ13,subQ1]),TD([makeQuery(id+"F6.opExtrude","CAP_FACE",FACE,{"disambiguationData":[OSD([subQ12,sQuery(id+"F5.wireOp",EDGE,"E34.0"),sQuery(id+"F5.wireOp",EDGE,"E38"),subQ0])],"isStart":true})])],"derivedFrom":subQ14}),makeQuery(id+"F6.boolean.opBoolean","SPLIT",EDGE,{"disambiguationData":[topologyDisambiguationEdgeConnected([subQ11,subQ13])],"derivedFrom":subQ14}),makeQuery(id+"F16.opExtrude","SWEPT_EDGE",EDGE,{"disambiguationData":[OSD([subQ9,subQ8,subQ7,subQ6,subQ5,subQ4,subQ3,subQ2,subQ0]),TDD([makeQuery(id+"F6.boolean.opBoolean","INTERSECT",VERTEX,{"disambiguationData":[OD(1.0)],"derivedFrom":[subQ10,subQ1]})])]})]});}
            var Q7;
            {var subQ0=sQuery(id+"F5.wireOp",EDGE,"E41");var subQ1=makeQuery(id+"F6.opExtrude","SWEPT_FACE",FACE,{"disambiguationData":[OSD([subQ0])]});var subQ2=sQuery(id+"F0.wireOp",EDGE,"E5.right");var subQ3=sQuery(id+"F0.wireOp",EDGE,"E5.left");var subQ4=sQuery(id+"F0.wireOp",EDGE,"E5.top");var subQ5=sQuery(id+"F0.wireOp",EDGE,"E5.bottom");var subQ6=sQuery(id+"F0.wireOp",EDGE,"E4");var subQ7=sQuery(id+"F0.wireOp",EDGE,"E3");var subQ8=sQuery(id+"F0.wireOp",EDGE,"E2");var subQ9=sQuery(id+"F0.wireOp",EDGE,"E1");var subQ10=makeQuery(id+"F1.opExtrude","CAP_FACE",FACE,{"disambiguationData":[OSD([subQ9,subQ8,subQ7,subQ6,subQ5,subQ4,subQ3,subQ2])],"isStart":true});var subQ11=makeQuery(id+"F1.opExtrude","SWEPT_FACE",FACE,{"disambiguationData":[OSD([subQ2])]});var subQ12=sQuery(id+"F5.wireOp",EDGE,"E32.0");var subQ13=makeQuery(id+"F6.opExtrude","SWEPT_FACE",FACE,{"disambiguationData":[OSD([subQ12])]});var subQ14=makeQuery(id+"F6.opExtrude","SWEPT_EDGE",EDGE,{"disambiguationData":[OSD([subQ12,subQ0])]});Q7=makeQuery(id+"F16.boolean.opBoolean","MERGE",EDGE,{"derivedFrom":[makeQuery(id+"F6.boolean.opBoolean","SPLIT",EDGE,{"disambiguationData":[topologyDisambiguationEdgeConnected([subQ13,subQ1]),TD([makeQuery(id+"F6.opExtrude","CAP_FACE",FACE,{"disambiguationData":[OSD([sQuery(id+"F5.wireOp",EDGE,"E31.1"),subQ12,sQuery(id+"F5.wireOp",EDGE,"E36"),subQ0])],"isStart":true})])],"derivedFrom":subQ14}),makeQuery(id+"F6.boolean.opBoolean","SPLIT",EDGE,{"disambiguationData":[topologyDisambiguationEdgeConnected([subQ11,subQ13])],"derivedFrom":subQ14}),makeQuery(id+"F16.opExtrude","SWEPT_EDGE",EDGE,{"disambiguationData":[OSD([subQ9,subQ8,subQ7,subQ6,subQ5,subQ4,subQ3,subQ2,subQ0]),TDD([makeQuery(id+"F6.boolean.opBoolean","INTERSECT",VERTEX,{"disambiguationData":[OD(1.0)],"derivedFrom":[subQ10,subQ1]})])]})]});}
            fillet(context, id + "F17", {"entities" : qUnion([Q0, Q1, Q2, Q3, Q4, Q5, Q6, Q7]), "radius" : 32.5 * mm, "tangentPropagation" : true, "allowEdgeOverflow" : false});
        }
        {
            var Q0;
            {var subQ0=sQuery(id+"F5.wireOp",EDGE,"E38");var subQ1=sQuery(id+"F5.wireOp",EDGE,"E33.0");Q0=makeQuery(id+"F7.boolean.opBoolean","MERGE",EDGE,{"derivedFrom":[makeQuery(id+"F6.opExtrude","CAP_EDGE",EDGE,{"disambiguationData":[OSD([subQ1])],"isStart":true}),makeQuery(id+"F7.opExtrude","SWEPT_EDGE",EDGE,{"disambiguationData":[OSD([subQ1,subQ0]),TDD([makeQuery(id+"F6.opExtrude","CAP_VERTEX",VERTEX,{"disambiguationData":[OSD([subQ1,subQ0])],"isStart":true})])]})]});}
            var Q1;
            {var subQ0=sQuery(id+"F5.wireOp",EDGE,"E38");var subQ1=sQuery(id+"F5.wireOp",EDGE,"E34.0");Q1=makeQuery(id+"F7.boolean.opBoolean","MERGE",EDGE,{"derivedFrom":[makeQuery(id+"F6.opExtrude","CAP_EDGE",EDGE,{"disambiguationData":[OSD([subQ1])],"isStart":true}),makeQuery(id+"F7.opExtrude","SWEPT_EDGE",EDGE,{"disambiguationData":[OSD([subQ1,subQ0]),TDD([makeQuery(id+"F6.opExtrude","CAP_VERTEX",VERTEX,{"disambiguationData":[OSD([subQ1,subQ0])],"isStart":true})])]})]});}
            var Q2;
            {var subQ0=sQuery(id+"F5.wireOp",EDGE,"E36");var subQ1=sQuery(id+"F5.wireOp",EDGE,"E32.0");Q2=makeQuery(id+"F8.boolean.opBoolean","MERGE",EDGE,{"derivedFrom":[makeQuery(id+"F6.opExtrude","CAP_EDGE",EDGE,{"disambiguationData":[OSD([subQ1])],"isStart":true}),makeQuery(id+"F8.opExtrude","SWEPT_EDGE",EDGE,{"disambiguationData":[OSD([subQ1,subQ0]),TDD([makeQuery(id+"F6.opExtrude","CAP_VERTEX",VERTEX,{"disambiguationData":[OSD([subQ1,subQ0])],"isStart":true})])]})]});}
            var Q3;
            {var subQ0=sQuery(id+"F5.wireOp",EDGE,"E36");var subQ1=sQuery(id+"F5.wireOp",EDGE,"E31.1");Q3=makeQuery(id+"F8.boolean.opBoolean","MERGE",EDGE,{"derivedFrom":[makeQuery(id+"F6.opExtrude","CAP_EDGE",EDGE,{"disambiguationData":[OSD([subQ1])],"isStart":true}),makeQuery(id+"F8.opExtrude","SWEPT_EDGE",EDGE,{"disambiguationData":[OSD([subQ1,subQ0]),TDD([makeQuery(id+"F6.opExtrude","CAP_VERTEX",VERTEX,{"disambiguationData":[OSD([subQ1,subQ0])],"isStart":true})])]})]});}
            var Q4;
            {var subQ0=sQuery(id+"F5.wireOp",EDGE,"E35");var subQ1=sQuery(id+"F5.wireOp",EDGE,"E33.1");Q4=makeQuery(id+"F9.boolean.opBoolean","MERGE",EDGE,{"derivedFrom":[makeQuery(id+"F6.opExtrude","CAP_EDGE",EDGE,{"disambiguationData":[OSD([subQ1])],"isStart":true}),makeQuery(id+"F9.opExtrude","SWEPT_EDGE",EDGE,{"disambiguationData":[OSD([subQ1,subQ0]),TDD([makeQuery(id+"F6.opExtrude","CAP_VERTEX",VERTEX,{"disambiguationData":[OSD([subQ1,subQ0])],"isStart":true})])]})]});}
            var Q5;
            {var subQ0=sQuery(id+"F5.wireOp",EDGE,"E35");var subQ1=sQuery(id+"F5.wireOp",EDGE,"E34.1");Q5=makeQuery(id+"F9.boolean.opBoolean","MERGE",EDGE,{"derivedFrom":[makeQuery(id+"F6.opExtrude","CAP_EDGE",EDGE,{"disambiguationData":[OSD([subQ1])],"isStart":true}),makeQuery(id+"F9.opExtrude","SWEPT_EDGE",EDGE,{"disambiguationData":[OSD([subQ1,subQ0]),TDD([makeQuery(id+"F6.opExtrude","CAP_VERTEX",VERTEX,{"disambiguationData":[OSD([subQ1,subQ0])],"isStart":true})])]})]});}
            var Q6;
            {var subQ0=sQuery(id+"F5.wireOp",EDGE,"E37");var subQ1=sQuery(id+"F5.wireOp",EDGE,"E31.0");Q6=makeQuery(id+"F10.boolean.opBoolean","MERGE",EDGE,{"derivedFrom":[makeQuery(id+"F6.opExtrude","CAP_EDGE",EDGE,{"disambiguationData":[OSD([subQ1])],"isStart":true}),makeQuery(id+"F10.opExtrude","SWEPT_EDGE",EDGE,{"disambiguationData":[OSD([subQ1,subQ0]),TDD([makeQuery(id+"F6.opExtrude","CAP_VERTEX",VERTEX,{"disambiguationData":[OSD([subQ1,subQ0])],"isStart":true})])]})]});}
            var Q7;
            {var subQ0=sQuery(id+"F5.wireOp",EDGE,"E37");var subQ1=sQuery(id+"F5.wireOp",EDGE,"E32.1");Q7=makeQuery(id+"F10.boolean.opBoolean","MERGE",EDGE,{"derivedFrom":[makeQuery(id+"F6.opExtrude","CAP_EDGE",EDGE,{"disambiguationData":[OSD([subQ1])],"isStart":true}),makeQuery(id+"F10.opExtrude","SWEPT_EDGE",EDGE,{"disambiguationData":[OSD([subQ1,subQ0]),TDD([makeQuery(id+"F6.opExtrude","CAP_VERTEX",VERTEX,{"disambiguationData":[OSD([subQ1,subQ0])],"isStart":true})])]})]});}
            fillet(context, id + "F18", {"entities" : qUnion([Q0, Q1, Q2, Q3, Q4, Q5, Q6, Q7]), "radius" : 6 * mm, "tangentPropagation" : true, "allowEdgeOverflow" : false});
        }
        {
            var Q0;
            {var subQ0=sQuery(id+"F0.wireOp",EDGE,"E5.right");var subQ1=sQuery(id+"F0.wireOp",EDGE,"E5.left");var subQ2=sQuery(id+"F0.wireOp",EDGE,"E5.top");var subQ3=sQuery(id+"F0.wireOp",EDGE,"E5.bottom");var subQ4=sQuery(id+"F0.wireOp",EDGE,"E4");var subQ5=sQuery(id+"F0.wireOp",EDGE,"E3");var subQ6=sQuery(id+"F0.wireOp",EDGE,"E2");var subQ7=sQuery(id+"F0.wireOp",EDGE,"E1");var subQ8=sQuery(id+"F5.wireOp",EDGE,"E40");var subQ9=makeQuery(id+"F6.opExtrude","SWEPT_FACE",FACE,{"disambiguationData":[OSD([subQ8])]});var subQ10=makeQuery(id+"F1.opExtrude","CAP_FACE",FACE,{"disambiguationData":[OSD([subQ7,subQ6,subQ5,subQ4,subQ3,subQ2,subQ1,subQ0])],"isStart":true});var subQ11=makeQuery(id+"F1.opExtrude","SWEPT_FACE",FACE,{"disambiguationData":[OSD([subQ1])]});var subQ12=sQuery(id+"F5.wireOp",EDGE,"E34.1");var subQ13=makeQuery(id+"F6.opExtrude","SWEPT_FACE",FACE,{"disambiguationData":[OSD([subQ12])]});var subQ14=makeQuery(id+"F6.opExtrude","SWEPT_EDGE",EDGE,{"disambiguationData":[OSD([subQ12,subQ8])]});Q0=makeQuery(id+"F17.opFillet","BLEND_EDGE",EDGE,{"blendedFrom":[makeQuery(id+"F16.boolean.opBoolean","MERGE",EDGE,{"derivedFrom":[makeQuery(id+"F6.boolean.opBoolean","SPLIT",EDGE,{"disambiguationData":[topologyDisambiguationEdgeConnected([subQ13,subQ9]),TD([makeQuery(id+"F6.opExtrude","CAP_FACE",FACE,{"disambiguationData":[OSD([sQuery(id+"F5.wireOp",EDGE,"E33.1"),subQ12,sQuery(id+"F5.wireOp",EDGE,"E35"),subQ8])],"isStart":true})])],"derivedFrom":subQ14}),makeQuery(id+"F6.boolean.opBoolean","SPLIT",EDGE,{"disambiguationData":[topologyDisambiguationEdgeConnected([subQ11,subQ13])],"derivedFrom":subQ14}),makeQuery(id+"F16.opExtrude","SWEPT_EDGE",EDGE,{"disambiguationData":[OSD([subQ7,subQ6,subQ5,subQ4,subQ3,subQ2,subQ1,subQ0,subQ8]),TDD([makeQuery(id+"F6.boolean.opBoolean","INTERSECT",VERTEX,{"disambiguationData":[OD(1.0)],"derivedFrom":[subQ10,subQ9]})])]})]}),makeQuery(id+"F1.opExtrude","CAP_FACE",FACE,{"disambiguationData":[OSD([subQ7,subQ6,subQ5,subQ4,subQ3,subQ2,subQ1,subQ0])],"isStart":false})],"blendedInto":[makeQuery(id+"F1.opExtrude","CAP_FACE",FACE,{"disambiguationData":[OSD([subQ7,subQ6,subQ5,subQ4,subQ3,subQ2,subQ1,subQ0])],"isStart":false})]});}
            var Q1;
            {var subQ0=sQuery(id+"F0.wireOp",EDGE,"E5.right");var subQ1=sQuery(id+"F0.wireOp",EDGE,"E5.left");var subQ2=sQuery(id+"F0.wireOp",EDGE,"E5.top");var subQ3=sQuery(id+"F0.wireOp",EDGE,"E5.bottom");var subQ4=sQuery(id+"F0.wireOp",EDGE,"E4");var subQ5=sQuery(id+"F0.wireOp",EDGE,"E3");var subQ6=sQuery(id+"F0.wireOp",EDGE,"E2");var subQ7=sQuery(id+"F0.wireOp",EDGE,"E1");var subQ8=sQuery(id+"F5.wireOp",EDGE,"E39");var subQ9=makeQuery(id+"F6.opExtrude","SWEPT_FACE",FACE,{"disambiguationData":[OSD([subQ8])]});var subQ10=makeQuery(id+"F1.opExtrude","CAP_FACE",FACE,{"disambiguationData":[OSD([subQ7,subQ6,subQ5,subQ4,subQ3,subQ2,subQ1,subQ0])],"isStart":true});var subQ11=makeQuery(id+"F1.opExtrude","SWEPT_FACE",FACE,{"disambiguationData":[OSD([subQ3])]});var subQ12=sQuery(id+"F5.wireOp",EDGE,"E32.1");var subQ13=makeQuery(id+"F6.opExtrude","SWEPT_FACE",FACE,{"disambiguationData":[OSD([subQ12])]});var subQ14=makeQuery(id+"F6.opExtrude","SWEPT_EDGE",EDGE,{"disambiguationData":[OSD([subQ12,subQ8])]});Q1=makeQuery(id+"F17.opFillet","BLEND_EDGE",EDGE,{"blendedFrom":[makeQuery(id+"F16.boolean.opBoolean","MERGE",EDGE,{"derivedFrom":[makeQuery(id+"F6.boolean.opBoolean","SPLIT",EDGE,{"disambiguationData":[topologyDisambiguationEdgeConnected([subQ13,subQ9]),TD([makeQuery(id+"F6.opExtrude","CAP_FACE",FACE,{"disambiguationData":[OSD([sQuery(id+"F5.wireOp",EDGE,"E31.0"),subQ12,sQuery(id+"F5.wireOp",EDGE,"E37"),subQ8])],"isStart":true})])],"derivedFrom":subQ14}),makeQuery(id+"F6.boolean.opBoolean","SPLIT",EDGE,{"disambiguationData":[topologyDisambiguationEdgeConnected([subQ11,subQ13])],"derivedFrom":subQ14}),makeQuery(id+"F16.opExtrude","SWEPT_EDGE",EDGE,{"disambiguationData":[OSD([subQ7,subQ6,subQ5,subQ4,subQ3,subQ2,subQ1,subQ0,subQ8]),TDD([makeQuery(id+"F6.boolean.opBoolean","INTERSECT",VERTEX,{"disambiguationData":[OD(0.0)],"derivedFrom":[subQ10,subQ9]})])]})]}),makeQuery(id+"F1.opExtrude","CAP_FACE",FACE,{"disambiguationData":[OSD([subQ7,subQ6,subQ5,subQ4,subQ3,subQ2,subQ1,subQ0])],"isStart":false})],"blendedInto":[makeQuery(id+"F1.opExtrude","CAP_FACE",FACE,{"disambiguationData":[OSD([subQ7,subQ6,subQ5,subQ4,subQ3,subQ2,subQ1,subQ0])],"isStart":false})]});}
            var Q2;
            {var subQ0=sQuery(id+"F0.wireOp",EDGE,"E5.right");var subQ1=sQuery(id+"F0.wireOp",EDGE,"E5.left");var subQ2=sQuery(id+"F0.wireOp",EDGE,"E5.top");var subQ3=sQuery(id+"F0.wireOp",EDGE,"E5.bottom");var subQ4=sQuery(id+"F0.wireOp",EDGE,"E4");var subQ5=sQuery(id+"F0.wireOp",EDGE,"E3");var subQ6=sQuery(id+"F0.wireOp",EDGE,"E2");var subQ7=sQuery(id+"F0.wireOp",EDGE,"E1");var subQ8=sQuery(id+"F5.wireOp",EDGE,"E42");var subQ9=makeQuery(id+"F6.opExtrude","SWEPT_FACE",FACE,{"disambiguationData":[OSD([subQ8])]});var subQ10=makeQuery(id+"F1.opExtrude","CAP_FACE",FACE,{"disambiguationData":[OSD([subQ7,subQ6,subQ5,subQ4,subQ3,subQ2,subQ1,subQ0])],"isStart":true});var subQ11=makeQuery(id+"F1.opExtrude","SWEPT_FACE",FACE,{"disambiguationData":[OSD([subQ0])]});var subQ12=sQuery(id+"F5.wireOp",EDGE,"E33.0");var subQ13=makeQuery(id+"F6.opExtrude","SWEPT_FACE",FACE,{"disambiguationData":[OSD([subQ12])]});var subQ14=makeQuery(id+"F6.opExtrude","SWEPT_EDGE",EDGE,{"disambiguationData":[OSD([subQ12,subQ8])]});Q2=makeQuery(id+"F17.opFillet","BLEND_EDGE",EDGE,{"blendedFrom":[makeQuery(id+"F16.boolean.opBoolean","MERGE",EDGE,{"derivedFrom":[makeQuery(id+"F6.boolean.opBoolean","SPLIT",EDGE,{"disambiguationData":[topologyDisambiguationEdgeConnected([subQ13,subQ9]),TD([makeQuery(id+"F6.opExtrude","CAP_FACE",FACE,{"disambiguationData":[OSD([subQ12,sQuery(id+"F5.wireOp",EDGE,"E34.0"),sQuery(id+"F5.wireOp",EDGE,"E38"),subQ8])],"isStart":true})])],"derivedFrom":subQ14}),makeQuery(id+"F6.boolean.opBoolean","SPLIT",EDGE,{"disambiguationData":[topologyDisambiguationEdgeConnected([subQ11,subQ13])],"derivedFrom":subQ14}),makeQuery(id+"F16.opExtrude","SWEPT_EDGE",EDGE,{"disambiguationData":[OSD([subQ7,subQ6,subQ5,subQ4,subQ3,subQ2,subQ1,subQ0,subQ8]),TDD([makeQuery(id+"F6.boolean.opBoolean","INTERSECT",VERTEX,{"disambiguationData":[OD(1.0)],"derivedFrom":[subQ10,subQ9]})])]})]}),makeQuery(id+"F1.opExtrude","CAP_FACE",FACE,{"disambiguationData":[OSD([subQ7,subQ6,subQ5,subQ4,subQ3,subQ2,subQ1,subQ0])],"isStart":false})],"blendedInto":[makeQuery(id+"F1.opExtrude","CAP_FACE",FACE,{"disambiguationData":[OSD([subQ7,subQ6,subQ5,subQ4,subQ3,subQ2,subQ1,subQ0])],"isStart":false})]});}
            var Q3;
            {var subQ0=sQuery(id+"F0.wireOp",EDGE,"E5.right");var subQ1=sQuery(id+"F0.wireOp",EDGE,"E5.left");var subQ2=sQuery(id+"F0.wireOp",EDGE,"E5.top");var subQ3=sQuery(id+"F0.wireOp",EDGE,"E5.bottom");var subQ4=sQuery(id+"F0.wireOp",EDGE,"E4");var subQ5=sQuery(id+"F0.wireOp",EDGE,"E3");var subQ6=sQuery(id+"F0.wireOp",EDGE,"E2");var subQ7=sQuery(id+"F0.wireOp",EDGE,"E1");var subQ8=sQuery(id+"F5.wireOp",EDGE,"E41");var subQ9=makeQuery(id+"F6.opExtrude","SWEPT_FACE",FACE,{"disambiguationData":[OSD([subQ8])]});var subQ10=makeQuery(id+"F1.opExtrude","CAP_FACE",FACE,{"disambiguationData":[OSD([subQ7,subQ6,subQ5,subQ4,subQ3,subQ2,subQ1,subQ0])],"isStart":true});var subQ11=makeQuery(id+"F1.opExtrude","SWEPT_FACE",FACE,{"disambiguationData":[OSD([subQ2])]});var subQ12=sQuery(id+"F5.wireOp",EDGE,"E31.1");var subQ13=makeQuery(id+"F6.opExtrude","SWEPT_FACE",FACE,{"disambiguationData":[OSD([subQ12])]});var subQ14=makeQuery(id+"F6.opExtrude","SWEPT_EDGE",EDGE,{"disambiguationData":[OSD([subQ12,subQ8])]});Q3=makeQuery(id+"F17.opFillet","BLEND_EDGE",EDGE,{"blendedFrom":[makeQuery(id+"F16.boolean.opBoolean","MERGE",EDGE,{"derivedFrom":[makeQuery(id+"F6.boolean.opBoolean","SPLIT",EDGE,{"disambiguationData":[topologyDisambiguationEdgeConnected([subQ13,subQ9]),TD([makeQuery(id+"F6.opExtrude","CAP_FACE",FACE,{"disambiguationData":[OSD([subQ12,sQuery(id+"F5.wireOp",EDGE,"E32.0"),sQuery(id+"F5.wireOp",EDGE,"E36"),subQ8])],"isStart":true})])],"derivedFrom":subQ14}),makeQuery(id+"F6.boolean.opBoolean","SPLIT",EDGE,{"disambiguationData":[topologyDisambiguationEdgeConnected([subQ11,subQ13])],"derivedFrom":subQ14}),makeQuery(id+"F16.opExtrude","SWEPT_EDGE",EDGE,{"disambiguationData":[OSD([subQ7,subQ6,subQ5,subQ4,subQ3,subQ2,subQ1,subQ0,subQ8]),TDD([makeQuery(id+"F6.boolean.opBoolean","INTERSECT",VERTEX,{"disambiguationData":[OD(0.0)],"derivedFrom":[subQ10,subQ9]})])]})]}),makeQuery(id+"F1.opExtrude","CAP_FACE",FACE,{"disambiguationData":[OSD([subQ7,subQ6,subQ5,subQ4,subQ3,subQ2,subQ1,subQ0])],"isStart":false})],"blendedInto":[makeQuery(id+"F1.opExtrude","CAP_FACE",FACE,{"disambiguationData":[OSD([subQ7,subQ6,subQ5,subQ4,subQ3,subQ2,subQ1,subQ0])],"isStart":false})]});}
            fillet(context, id + "F19", {"entities" : qUnion([Q0, Q1, Q2, Q3]), "radius" : 2.5 * mm, "tangentPropagation" : true, "allowEdgeOverflow" : false});
        }
        {
            var Q0;
            {var subQ0=sQuery(id+"F5.wireOp",EDGE,"E38");var subQ1=sQuery(id+"F5.wireOp",EDGE,"E33.0");Q0=makeQuery(id+"F7.boolean.opBoolean","MERGE",EDGE,{"derivedFrom":[makeQuery(id+"F6.opExtrude","CAP_EDGE",EDGE,{"disambiguationData":[OSD([subQ1])],"isStart":false}),makeQuery(id+"F7.opExtrude","SWEPT_EDGE",EDGE,{"disambiguationData":[OSD([subQ1,subQ0]),TDD([makeQuery(id+"F6.opExtrude","CAP_VERTEX",VERTEX,{"disambiguationData":[OSD([subQ1,subQ0])],"isStart":false})])]})]});}
            var Q1;
            {var subQ0=sQuery(id+"F5.wireOp",EDGE,"E38");var subQ1=sQuery(id+"F5.wireOp",EDGE,"E34.0");Q1=makeQuery(id+"F7.boolean.opBoolean","MERGE",EDGE,{"derivedFrom":[makeQuery(id+"F6.opExtrude","CAP_EDGE",EDGE,{"disambiguationData":[OSD([subQ1])],"isStart":false}),makeQuery(id+"F7.opExtrude","SWEPT_EDGE",EDGE,{"disambiguationData":[OSD([subQ1,subQ0]),TDD([makeQuery(id+"F6.opExtrude","CAP_VERTEX",VERTEX,{"disambiguationData":[OSD([subQ1,subQ0])],"isStart":false})])]})]});}
            var Q2;
            {var subQ0=sQuery(id+"F5.wireOp",EDGE,"E37");var subQ1=sQuery(id+"F5.wireOp",EDGE,"E32.1");Q2=makeQuery(id+"F10.boolean.opBoolean","MERGE",EDGE,{"derivedFrom":[makeQuery(id+"F6.opExtrude","CAP_EDGE",EDGE,{"disambiguationData":[OSD([subQ1])],"isStart":false}),makeQuery(id+"F10.opExtrude","SWEPT_EDGE",EDGE,{"disambiguationData":[OSD([subQ1,subQ0]),TDD([makeQuery(id+"F6.opExtrude","CAP_VERTEX",VERTEX,{"disambiguationData":[OSD([subQ1,subQ0])],"isStart":false})])]})]});}
            var Q3;
            {var subQ0=sQuery(id+"F5.wireOp",EDGE,"E37");var subQ1=sQuery(id+"F5.wireOp",EDGE,"E31.0");Q3=makeQuery(id+"F10.boolean.opBoolean","MERGE",EDGE,{"derivedFrom":[makeQuery(id+"F6.opExtrude","CAP_EDGE",EDGE,{"disambiguationData":[OSD([subQ1])],"isStart":false}),makeQuery(id+"F10.opExtrude","SWEPT_EDGE",EDGE,{"disambiguationData":[OSD([subQ1,subQ0]),TDD([makeQuery(id+"F6.opExtrude","CAP_VERTEX",VERTEX,{"disambiguationData":[OSD([subQ1,subQ0])],"isStart":false})])]})]});}
            var Q4;
            {var subQ0=sQuery(id+"F5.wireOp",EDGE,"E35");var subQ1=sQuery(id+"F5.wireOp",EDGE,"E34.1");Q4=makeQuery(id+"F9.boolean.opBoolean","MERGE",EDGE,{"derivedFrom":[makeQuery(id+"F6.opExtrude","CAP_EDGE",EDGE,{"disambiguationData":[OSD([subQ1])],"isStart":false}),makeQuery(id+"F9.opExtrude","SWEPT_EDGE",EDGE,{"disambiguationData":[OSD([subQ1,subQ0]),TDD([makeQuery(id+"F6.opExtrude","CAP_VERTEX",VERTEX,{"disambiguationData":[OSD([subQ1,subQ0])],"isStart":false})])]})]});}
            var Q5;
            {var subQ0=sQuery(id+"F5.wireOp",EDGE,"E35");var subQ1=sQuery(id+"F5.wireOp",EDGE,"E33.1");Q5=makeQuery(id+"F9.boolean.opBoolean","MERGE",EDGE,{"derivedFrom":[makeQuery(id+"F6.opExtrude","CAP_EDGE",EDGE,{"disambiguationData":[OSD([subQ1])],"isStart":false}),makeQuery(id+"F9.opExtrude","SWEPT_EDGE",EDGE,{"disambiguationData":[OSD([subQ1,subQ0]),TDD([makeQuery(id+"F6.opExtrude","CAP_VERTEX",VERTEX,{"disambiguationData":[OSD([subQ1,subQ0])],"isStart":false})])]})]});}
            var Q6;
            {var subQ0=sQuery(id+"F5.wireOp",EDGE,"E36");var subQ1=sQuery(id+"F5.wireOp",EDGE,"E31.1");Q6=makeQuery(id+"F8.boolean.opBoolean","MERGE",EDGE,{"derivedFrom":[makeQuery(id+"F6.opExtrude","CAP_EDGE",EDGE,{"disambiguationData":[OSD([subQ1])],"isStart":false}),makeQuery(id+"F8.opExtrude","SWEPT_EDGE",EDGE,{"disambiguationData":[OSD([subQ1,subQ0]),TDD([makeQuery(id+"F6.opExtrude","CAP_VERTEX",VERTEX,{"disambiguationData":[OSD([subQ1,subQ0])],"isStart":false})])]})]});}
            var Q7;
            {var subQ0=sQuery(id+"F5.wireOp",EDGE,"E36");var subQ1=sQuery(id+"F5.wireOp",EDGE,"E32.0");Q7=makeQuery(id+"F8.boolean.opBoolean","MERGE",EDGE,{"derivedFrom":[makeQuery(id+"F6.opExtrude","CAP_EDGE",EDGE,{"disambiguationData":[OSD([subQ1])],"isStart":false}),makeQuery(id+"F8.opExtrude","SWEPT_EDGE",EDGE,{"disambiguationData":[OSD([subQ1,subQ0]),TDD([makeQuery(id+"F6.opExtrude","CAP_VERTEX",VERTEX,{"disambiguationData":[OSD([subQ1,subQ0])],"isStart":false})])]})]});}
            fillet(context, id + "F20", {"entities" : qUnion([Q0, Q1, Q2, Q3, Q4, Q5, Q6, Q7]), "radius" : 6 * mm, "tangentPropagation" : true, "allowEdgeOverflow" : false});
        }
        {
            var Q0;
            {var subQ1=sQuery(id+"F5.wireOp",EDGE,"E42");var subQ2=sQuery(id+"F5.wireOp",EDGE,"E38");var subQ3=sQuery(id+"F5.wireOp",EDGE,"E34.0");var subQ4=sQuery(id+"F5.wireOp",EDGE,"E33.0");Q0=makeQuery(id+"F20.opFillet","BLEND_EDGE",EDGE,{"blendedFrom":[makeQuery(id+"F7.boolean.opBoolean","MERGE",EDGE,{"derivedFrom":[makeQuery(id+"F6.opExtrude","CAP_EDGE",EDGE,{"disambiguationData":[OSD([subQ4])],"isStart":false}),makeQuery(id+"F7.opExtrude","SWEPT_EDGE",EDGE,{"disambiguationData":[OSD([subQ4,subQ2]),TDD([makeQuery(id+"F6.opExtrude","CAP_VERTEX",VERTEX,{"disambiguationData":[OSD([subQ4,subQ2])],"isStart":false})])]})]}),makeQuery(id+"F6.boolean.opBoolean","SPLIT",FACE,{"disambiguationData":[TD([makeQuery(id+"F6.opExtrude","CAP_FACE",FACE,{"disambiguationData":[OSD([subQ4,subQ3,subQ2,subQ1])],"isStart":false})])],"derivedFrom":makeQuery(id+"F6.opExtrude","SWEPT_FACE",FACE,{"disambiguationData":[OSD([subQ1])]})})],"blendedInto":[makeQuery(id+"F6.boolean.opBoolean","SPLIT",FACE,{"disambiguationData":[TD([makeQuery(id+"F6.opExtrude","CAP_FACE",FACE,{"disambiguationData":[OSD([subQ4,subQ3,subQ2,subQ1])],"isStart":false})])],"derivedFrom":makeQuery(id+"F6.opExtrude","SWEPT_FACE",FACE,{"disambiguationData":[OSD([subQ1])]})})]});}
            var Q1;
            {var subQ0=sQuery(id+"F5.wireOp",EDGE,"E31.0");var subQ3=sQuery(id+"F5.wireOp",EDGE,"E32.1");var subQ4=sQuery(id+"F5.wireOp",EDGE,"E39");var subQ5=sQuery(id+"F5.wireOp",EDGE,"E37");Q1=makeQuery(id+"F20.opFillet","BLEND_EDGE",EDGE,{"blendedFrom":[makeQuery(id+"F10.boolean.opBoolean","MERGE",EDGE,{"derivedFrom":[makeQuery(id+"F6.opExtrude","CAP_EDGE",EDGE,{"disambiguationData":[OSD([subQ3])],"isStart":false}),makeQuery(id+"F10.opExtrude","SWEPT_EDGE",EDGE,{"disambiguationData":[OSD([subQ3,subQ5]),TDD([makeQuery(id+"F6.opExtrude","CAP_VERTEX",VERTEX,{"disambiguationData":[OSD([subQ3,subQ5])],"isStart":false})])]})]}),makeQuery(id+"F6.boolean.opBoolean","SPLIT",FACE,{"disambiguationData":[TD([makeQuery(id+"F6.opExtrude","CAP_FACE",FACE,{"disambiguationData":[OSD([subQ0,subQ3,subQ5,subQ4])],"isStart":false})])],"derivedFrom":makeQuery(id+"F6.opExtrude","SWEPT_FACE",FACE,{"disambiguationData":[OSD([subQ4])]})})],"blendedInto":[makeQuery(id+"F6.boolean.opBoolean","SPLIT",FACE,{"disambiguationData":[TD([makeQuery(id+"F6.opExtrude","CAP_FACE",FACE,{"disambiguationData":[OSD([subQ0,subQ3,subQ5,subQ4])],"isStart":false})])],"derivedFrom":makeQuery(id+"F6.opExtrude","SWEPT_FACE",FACE,{"disambiguationData":[OSD([subQ4])]})})]});}
            var Q2;
            {var subQ0=sQuery(id+"F5.wireOp",EDGE,"E31.1");var subQ3=sQuery(id+"F5.wireOp",EDGE,"E41");var subQ4=sQuery(id+"F5.wireOp",EDGE,"E36");var subQ5=sQuery(id+"F5.wireOp",EDGE,"E32.0");Q2=makeQuery(id+"F20.opFillet","BLEND_EDGE",EDGE,{"blendedFrom":[makeQuery(id+"F8.boolean.opBoolean","MERGE",EDGE,{"derivedFrom":[makeQuery(id+"F6.opExtrude","CAP_EDGE",EDGE,{"disambiguationData":[OSD([subQ5])],"isStart":false}),makeQuery(id+"F8.opExtrude","SWEPT_EDGE",EDGE,{"disambiguationData":[OSD([subQ5,subQ4]),TDD([makeQuery(id+"F6.opExtrude","CAP_VERTEX",VERTEX,{"disambiguationData":[OSD([subQ5,subQ4])],"isStart":false})])]})]}),makeQuery(id+"F6.boolean.opBoolean","SPLIT",FACE,{"disambiguationData":[TD([makeQuery(id+"F6.opExtrude","CAP_FACE",FACE,{"disambiguationData":[OSD([subQ0,subQ5,subQ4,subQ3])],"isStart":false})])],"derivedFrom":makeQuery(id+"F6.opExtrude","SWEPT_FACE",FACE,{"disambiguationData":[OSD([subQ3])]})})],"blendedInto":[makeQuery(id+"F6.boolean.opBoolean","SPLIT",FACE,{"disambiguationData":[TD([makeQuery(id+"F6.opExtrude","CAP_FACE",FACE,{"disambiguationData":[OSD([subQ0,subQ5,subQ4,subQ3])],"isStart":false})])],"derivedFrom":makeQuery(id+"F6.opExtrude","SWEPT_FACE",FACE,{"disambiguationData":[OSD([subQ3])]})})]});}
            var Q3;
            {var subQ0=sQuery(id+"F5.wireOp",EDGE,"E33.1");var subQ3=sQuery(id+"F5.wireOp",EDGE,"E40");var subQ4=sQuery(id+"F5.wireOp",EDGE,"E35");var subQ5=sQuery(id+"F5.wireOp",EDGE,"E34.1");Q3=makeQuery(id+"F20.opFillet","BLEND_EDGE",EDGE,{"blendedFrom":[makeQuery(id+"F9.boolean.opBoolean","MERGE",EDGE,{"derivedFrom":[makeQuery(id+"F6.opExtrude","CAP_EDGE",EDGE,{"disambiguationData":[OSD([subQ0])],"isStart":false}),makeQuery(id+"F9.opExtrude","SWEPT_EDGE",EDGE,{"disambiguationData":[OSD([subQ0,subQ4]),TDD([makeQuery(id+"F6.opExtrude","CAP_VERTEX",VERTEX,{"disambiguationData":[OSD([subQ0,subQ4])],"isStart":false})])]})]}),makeQuery(id+"F6.boolean.opBoolean","SPLIT",FACE,{"disambiguationData":[TD([makeQuery(id+"F6.opExtrude","CAP_FACE",FACE,{"disambiguationData":[OSD([subQ0,subQ5,subQ4,subQ3])],"isStart":false})])],"derivedFrom":makeQuery(id+"F6.opExtrude","SWEPT_FACE",FACE,{"disambiguationData":[OSD([subQ3])]})})],"blendedInto":[makeQuery(id+"F6.boolean.opBoolean","SPLIT",FACE,{"disambiguationData":[TD([makeQuery(id+"F6.opExtrude","CAP_FACE",FACE,{"disambiguationData":[OSD([subQ0,subQ5,subQ4,subQ3])],"isStart":false})])],"derivedFrom":makeQuery(id+"F6.opExtrude","SWEPT_FACE",FACE,{"disambiguationData":[OSD([subQ3])]})})]});}
            fillet(context, id + "F21", {"entities" : qUnion([Q0, Q1, Q2, Q3]), "radius" : 3.5 * mm, "tangentPropagation" : true, "allowEdgeOverflow" : false});
        }
        {
            var Q0;
            {var subQ0=sQuery(id+"F0.wireOp",EDGE,"E5.right");var subQ1=sQuery(id+"F0.wireOp",EDGE,"E5.bottom");var subQ2=makeQuery(id+"F1.opExtrude","CAP_FACE",FACE,{"disambiguationData":[OSD([sQuery(id+"F0.wireOp",EDGE,"E1"),sQuery(id+"F0.wireOp",EDGE,"E2"),sQuery(id+"F0.wireOp",EDGE,"E3"),sQuery(id+"F0.wireOp",EDGE,"E4"),subQ1,sQuery(id+"F0.wireOp",EDGE,"E5.top"),sQuery(id+"F0.wireOp",EDGE,"E5.left"),subQ0])],"isStart":false});var subQ3=sQuery(id+"F5.wireOp",EDGE,"E42");var subQ4=sQuery(id+"F5.wireOp",EDGE,"E38");var subQ5=sQuery(id+"F5.wireOp",EDGE,"E34.0");var subQ6=sQuery(id+"F5.wireOp",EDGE,"E33.0");Q0=makeQuery(id+"F21.opFillet","BLEND_EDGE",EDGE,{"disambiguationData":[OD(1.0)],"blendedFrom":[makeQuery(id+"F20.opFillet","BLEND_EDGE",EDGE,{"blendedFrom":[makeQuery(id+"F7.boolean.opBoolean","MERGE",EDGE,{"derivedFrom":[makeQuery(id+"F6.opExtrude","CAP_EDGE",EDGE,{"disambiguationData":[OSD([subQ6])],"isStart":false}),makeQuery(id+"F7.opExtrude","SWEPT_EDGE",EDGE,{"disambiguationData":[OSD([subQ6,subQ4]),TDD([makeQuery(id+"F6.opExtrude","CAP_VERTEX",VERTEX,{"disambiguationData":[OSD([subQ6,subQ4])],"isStart":false})])]})]}),makeQuery(id+"F6.boolean.opBoolean","SPLIT",FACE,{"disambiguationData":[TD([makeQuery(id+"F6.opExtrude","CAP_FACE",FACE,{"disambiguationData":[OSD([subQ6,subQ5,subQ4,subQ3])],"isStart":false})])],"derivedFrom":makeQuery(id+"F6.opExtrude","SWEPT_FACE",FACE,{"disambiguationData":[OSD([subQ3])]})})],"blendedInto":[makeQuery(id+"F6.boolean.opBoolean","SPLIT",FACE,{"disambiguationData":[TD([makeQuery(id+"F6.opExtrude","CAP_FACE",FACE,{"disambiguationData":[OSD([subQ6,subQ5,subQ4,subQ3])],"isStart":false})])],"derivedFrom":makeQuery(id+"F6.opExtrude","SWEPT_FACE",FACE,{"disambiguationData":[OSD([subQ3])]})})]}),subQ2],"blendedInto":[subQ2]});}
            var Q1;
            {var subQ0=sQuery(id+"F0.wireOp",EDGE,"E5.left");var subQ1=sQuery(id+"F0.wireOp",EDGE,"E5.bottom");var subQ2=makeQuery(id+"F1.opExtrude","CAP_FACE",FACE,{"disambiguationData":[OSD([sQuery(id+"F0.wireOp",EDGE,"E1"),sQuery(id+"F0.wireOp",EDGE,"E2"),sQuery(id+"F0.wireOp",EDGE,"E3"),sQuery(id+"F0.wireOp",EDGE,"E4"),subQ1,sQuery(id+"F0.wireOp",EDGE,"E5.top"),subQ0,sQuery(id+"F0.wireOp",EDGE,"E5.right")])],"isStart":false});var subQ3=sQuery(id+"F5.wireOp",EDGE,"E31.0");var subQ4=sQuery(id+"F5.wireOp",EDGE,"E32.1");var subQ5=sQuery(id+"F5.wireOp",EDGE,"E39");var subQ6=sQuery(id+"F5.wireOp",EDGE,"E37");Q1=makeQuery(id+"F21.opFillet","BLEND_EDGE",EDGE,{"disambiguationData":[OD(1.0)],"blendedFrom":[makeQuery(id+"F20.opFillet","BLEND_EDGE",EDGE,{"blendedFrom":[makeQuery(id+"F10.boolean.opBoolean","MERGE",EDGE,{"derivedFrom":[makeQuery(id+"F6.opExtrude","CAP_EDGE",EDGE,{"disambiguationData":[OSD([subQ4])],"isStart":false}),makeQuery(id+"F10.opExtrude","SWEPT_EDGE",EDGE,{"disambiguationData":[OSD([subQ4,subQ6]),TDD([makeQuery(id+"F6.opExtrude","CAP_VERTEX",VERTEX,{"disambiguationData":[OSD([subQ4,subQ6])],"isStart":false})])]})]}),makeQuery(id+"F6.boolean.opBoolean","SPLIT",FACE,{"disambiguationData":[TD([makeQuery(id+"F6.opExtrude","CAP_FACE",FACE,{"disambiguationData":[OSD([subQ3,subQ4,subQ6,subQ5])],"isStart":false})])],"derivedFrom":makeQuery(id+"F6.opExtrude","SWEPT_FACE",FACE,{"disambiguationData":[OSD([subQ5])]})})],"blendedInto":[makeQuery(id+"F6.boolean.opBoolean","SPLIT",FACE,{"disambiguationData":[TD([makeQuery(id+"F6.opExtrude","CAP_FACE",FACE,{"disambiguationData":[OSD([subQ3,subQ4,subQ6,subQ5])],"isStart":false})])],"derivedFrom":makeQuery(id+"F6.opExtrude","SWEPT_FACE",FACE,{"disambiguationData":[OSD([subQ5])]})})]}),subQ2],"blendedInto":[subQ2]});}
            var Q2;
            {var subQ0=sQuery(id+"F0.wireOp",EDGE,"E5.left");var subQ1=sQuery(id+"F0.wireOp",EDGE,"E5.top");var subQ2=makeQuery(id+"F1.opExtrude","CAP_FACE",FACE,{"disambiguationData":[OSD([sQuery(id+"F0.wireOp",EDGE,"E1"),sQuery(id+"F0.wireOp",EDGE,"E2"),sQuery(id+"F0.wireOp",EDGE,"E3"),sQuery(id+"F0.wireOp",EDGE,"E4"),sQuery(id+"F0.wireOp",EDGE,"E5.bottom"),subQ1,subQ0,sQuery(id+"F0.wireOp",EDGE,"E5.right")])],"isStart":false});var subQ3=sQuery(id+"F5.wireOp",EDGE,"E33.1");var subQ4=sQuery(id+"F5.wireOp",EDGE,"E40");var subQ5=sQuery(id+"F5.wireOp",EDGE,"E35");var subQ6=sQuery(id+"F5.wireOp",EDGE,"E34.1");Q2=makeQuery(id+"F21.opFillet","BLEND_EDGE",EDGE,{"disambiguationData":[OD(0.0)],"blendedFrom":[makeQuery(id+"F20.opFillet","BLEND_EDGE",EDGE,{"blendedFrom":[makeQuery(id+"F9.boolean.opBoolean","MERGE",EDGE,{"derivedFrom":[makeQuery(id+"F6.opExtrude","CAP_EDGE",EDGE,{"disambiguationData":[OSD([subQ3])],"isStart":false}),makeQuery(id+"F9.opExtrude","SWEPT_EDGE",EDGE,{"disambiguationData":[OSD([subQ3,subQ5]),TDD([makeQuery(id+"F6.opExtrude","CAP_VERTEX",VERTEX,{"disambiguationData":[OSD([subQ3,subQ5])],"isStart":false})])]})]}),makeQuery(id+"F6.boolean.opBoolean","SPLIT",FACE,{"disambiguationData":[TD([makeQuery(id+"F6.opExtrude","CAP_FACE",FACE,{"disambiguationData":[OSD([subQ3,subQ6,subQ5,subQ4])],"isStart":false})])],"derivedFrom":makeQuery(id+"F6.opExtrude","SWEPT_FACE",FACE,{"disambiguationData":[OSD([subQ4])]})})],"blendedInto":[makeQuery(id+"F6.boolean.opBoolean","SPLIT",FACE,{"disambiguationData":[TD([makeQuery(id+"F6.opExtrude","CAP_FACE",FACE,{"disambiguationData":[OSD([subQ3,subQ6,subQ5,subQ4])],"isStart":false})])],"derivedFrom":makeQuery(id+"F6.opExtrude","SWEPT_FACE",FACE,{"disambiguationData":[OSD([subQ4])]})})]}),subQ2],"blendedInto":[subQ2]});}
            var Q3;
            {var subQ0=sQuery(id+"F0.wireOp",EDGE,"E5.right");var subQ1=sQuery(id+"F0.wireOp",EDGE,"E5.top");var subQ2=makeQuery(id+"F1.opExtrude","CAP_FACE",FACE,{"disambiguationData":[OSD([sQuery(id+"F0.wireOp",EDGE,"E1"),sQuery(id+"F0.wireOp",EDGE,"E2"),sQuery(id+"F0.wireOp",EDGE,"E3"),sQuery(id+"F0.wireOp",EDGE,"E4"),sQuery(id+"F0.wireOp",EDGE,"E5.bottom"),subQ1,sQuery(id+"F0.wireOp",EDGE,"E5.left"),subQ0])],"isStart":false});var subQ3=sQuery(id+"F5.wireOp",EDGE,"E31.1");var subQ4=sQuery(id+"F5.wireOp",EDGE,"E41");var subQ5=sQuery(id+"F5.wireOp",EDGE,"E36");var subQ6=sQuery(id+"F5.wireOp",EDGE,"E32.0");Q3=makeQuery(id+"F21.opFillet","BLEND_EDGE",EDGE,{"disambiguationData":[OD(1.0)],"blendedFrom":[makeQuery(id+"F20.opFillet","BLEND_EDGE",EDGE,{"blendedFrom":[makeQuery(id+"F8.boolean.opBoolean","MERGE",EDGE,{"derivedFrom":[makeQuery(id+"F6.opExtrude","CAP_EDGE",EDGE,{"disambiguationData":[OSD([subQ6])],"isStart":false}),makeQuery(id+"F8.opExtrude","SWEPT_EDGE",EDGE,{"disambiguationData":[OSD([subQ6,subQ5]),TDD([makeQuery(id+"F6.opExtrude","CAP_VERTEX",VERTEX,{"disambiguationData":[OSD([subQ6,subQ5])],"isStart":false})])]})]}),makeQuery(id+"F6.boolean.opBoolean","SPLIT",FACE,{"disambiguationData":[TD([makeQuery(id+"F6.opExtrude","CAP_FACE",FACE,{"disambiguationData":[OSD([subQ3,subQ6,subQ5,subQ4])],"isStart":false})])],"derivedFrom":makeQuery(id+"F6.opExtrude","SWEPT_FACE",FACE,{"disambiguationData":[OSD([subQ4])]})})],"blendedInto":[makeQuery(id+"F6.boolean.opBoolean","SPLIT",FACE,{"disambiguationData":[TD([makeQuery(id+"F6.opExtrude","CAP_FACE",FACE,{"disambiguationData":[OSD([subQ3,subQ6,subQ5,subQ4])],"isStart":false})])],"derivedFrom":makeQuery(id+"F6.opExtrude","SWEPT_FACE",FACE,{"disambiguationData":[OSD([subQ4])]})})]}),subQ2],"blendedInto":[subQ2]});}
            fillet(context, id + "F22", {"entities" : qUnion([Q0, Q1, Q2, Q3]), "radius" : 5 * mm, "tangentPropagation" : true, "allowEdgeOverflow" : false});
        }
        {
            var Q0;
            {var subQ0=sQuery(id+"F5.wireOp",EDGE,"E39");var subQ1=sQuery(id+"F5.wireOp",EDGE,"E37");var subQ2=sQuery(id+"F5.wireOp",EDGE,"E32.1");var subQ3=sQuery(id+"F5.wireOp",EDGE,"E31.0");var subQ4=sQuery(id+"F5.wireOp",EDGE,"E35");var subQ5=sQuery(id+"F5.wireOp",EDGE,"E36");var subQ6=sQuery(id+"F5.wireOp",EDGE,"E38");Q0=makeQuery(id+"F16.boolean.opBoolean","MERGE",FACE,{"derivedFrom":[makeQuery(id+"F7.boolean.opBoolean","MERGE",FACE,{"derivedFrom":[makeQuery(id+"F6.opExtrude","CAP_FACE",FACE,{"disambiguationData":[OSD([sQuery(id+"F5.wireOp",EDGE,"E33.0"),sQuery(id+"F5.wireOp",EDGE,"E34.0"),subQ6,sQuery(id+"F5.wireOp",EDGE,"E42")])],"isStart":true}),makeQuery(id+"F7.opExtrude","SWEPT_FACE",FACE,{"disambiguationData":[OSD([subQ6]),TDD([makeQuery(id+"F6.opExtrude","CAP_EDGE",EDGE,{"disambiguationData":[OSD([subQ6])],"isStart":true})])]})]}),makeQuery(id+"F8.boolean.opBoolean","MERGE",FACE,{"derivedFrom":[makeQuery(id+"F6.opExtrude","CAP_FACE",FACE,{"disambiguationData":[OSD([sQuery(id+"F5.wireOp",EDGE,"E31.1"),sQuery(id+"F5.wireOp",EDGE,"E32.0"),subQ5,sQuery(id+"F5.wireOp",EDGE,"E41")])],"isStart":true}),makeQuery(id+"F8.opExtrude","SWEPT_FACE",FACE,{"disambiguationData":[OSD([subQ5]),TDD([makeQuery(id+"F6.opExtrude","CAP_EDGE",EDGE,{"disambiguationData":[OSD([subQ5])],"isStart":true})])]})]}),makeQuery(id+"F9.boolean.opBoolean","MERGE",FACE,{"derivedFrom":[makeQuery(id+"F6.opExtrude","CAP_FACE",FACE,{"disambiguationData":[OSD([sQuery(id+"F5.wireOp",EDGE,"E33.1"),sQuery(id+"F5.wireOp",EDGE,"E34.1"),subQ4,sQuery(id+"F5.wireOp",EDGE,"E40")])],"isStart":true}),makeQuery(id+"F9.opExtrude","SWEPT_FACE",FACE,{"disambiguationData":[OSD([subQ4]),TDD([makeQuery(id+"F6.opExtrude","CAP_EDGE",EDGE,{"disambiguationData":[OSD([subQ4])],"isStart":true})])]})]}),makeQuery(id+"F10.boolean.opBoolean","MERGE",FACE,{"derivedFrom":[makeQuery(id+"F6.opExtrude","CAP_FACE",FACE,{"disambiguationData":[OSD([subQ3,subQ2,subQ1,subQ0])],"isStart":true}),makeQuery(id+"F10.opExtrude","SWEPT_FACE",FACE,{"disambiguationData":[OSD([subQ1]),TDD([makeQuery(id+"F6.opExtrude","CAP_EDGE",EDGE,{"disambiguationData":[OSD([subQ1])],"isStart":true})])]})]}),makeQuery(id+"F16.opExtrude","CAP_FACE",FACE,{"disambiguationData":[OSD([subQ3,subQ2,subQ1,subQ0])],"isStart":false})]});}
            var sketch = newSketch(context, id + "F23", { "sketchPlane" : qUnion([Q0])});
            skCircle(sketch, "E51", {"center": v(15.25, 15.25) * mm, "radius": 3.5 * mm});
            skCircle(sketch, "E52", {"center": v(-15.25, 15.25) * mm, "radius": 3.5 * mm});
            skCircle(sketch, "E53", {"center": v(-15.25, -15.25) * mm, "radius": 3.5 * mm});
            skCircle(sketch, "E54", {"center": v(15.25, -15.25) * mm, "radius": 3.5 * mm});
            skSolve(sketch);
        }
        {
            var Q0;
            Q0=makeQuery(id+"F23.imprint","IMPRINT",FACE,{"disambiguationData":[TD([[makeQuery(id+"F23.imprint","IMPRINT",EDGE,{"derivedFrom":sQuery(id+"F23.wireOp",EDGE,"E52")}),1.0]])]});
            var Q1;
            Q1=makeQuery(id+"F23.imprint","IMPRINT",FACE,{"disambiguationData":[TD([[makeQuery(id+"F23.imprint","IMPRINT",EDGE,{"derivedFrom":sQuery(id+"F23.wireOp",EDGE,"E51")}),1.0]])]});
            var Q2;
            Q2=makeQuery(id+"F23.imprint","IMPRINT",FACE,{"disambiguationData":[TD([[makeQuery(id+"F23.imprint","IMPRINT",EDGE,{"derivedFrom":sQuery(id+"F23.wireOp",EDGE,"E53")}),1.0]])]});
            var Q3;
            Q3=makeQuery(id+"F23.imprint","IMPRINT",FACE,{"disambiguationData":[TD([[makeQuery(id+"F23.imprint","IMPRINT",EDGE,{"derivedFrom":sQuery(id+"F23.wireOp",EDGE,"E54")}),1.0]])]});
            extrude(context, id + "F24", {"entities" : qUnion([Q0, Q1, Q2, Q3]), "operationType" : NewBodyOperationType.REMOVE, "oppositeDirection" : true, "depth" : 4 * mm, "offsetDistance" : 25 * mm});
        }
        {
            var Q0;
            Q0=makeQuery(id+"F24.boolean.opBoolean","COPY",EDGE,{"derivedFrom":makeQuery(id+"F24.opExtrude","CAP_EDGE",EDGE,{"disambiguationData":[OSD([sQuery(id+"F23.wireOp",EDGE,"E52")])],"isStart":true})});
            var Q1;
            Q1=makeQuery(id+"F24.boolean.opBoolean","COPY",EDGE,{"derivedFrom":makeQuery(id+"F24.opExtrude","CAP_EDGE",EDGE,{"disambiguationData":[OSD([sQuery(id+"F23.wireOp",EDGE,"E51")])],"isStart":true})});
            var Q2;
            Q2=makeQuery(id+"F24.boolean.opBoolean","COPY",EDGE,{"derivedFrom":makeQuery(id+"F24.opExtrude","CAP_EDGE",EDGE,{"disambiguationData":[OSD([sQuery(id+"F23.wireOp",EDGE,"E53")])],"isStart":true})});
            var Q3;
            Q3=makeQuery(id+"F24.boolean.opBoolean","COPY",EDGE,{"derivedFrom":makeQuery(id+"F24.opExtrude","CAP_EDGE",EDGE,{"disambiguationData":[OSD([sQuery(id+"F23.wireOp",EDGE,"E54")])],"isStart":true})});
            fillet(context, id + "F25", {"entities" : qUnion([Q0, Q1, Q2, Q3]), "radius" : 1 * mm, "tangentPropagation" : true, "allowEdgeOverflow" : false});
        }
        {
            var Q0;
            {var subQ0=sQuery(id+"F5.wireOp",EDGE,"E36");var subQ1=sQuery(id+"F5.wireOp",EDGE,"E32.0");Q0=makeQuery(id+"F20.opFillet","BLEND_EDGE",EDGE,{"blendedFrom":[makeQuery(id+"F8.boolean.opBoolean","MERGE",EDGE,{"derivedFrom":[makeQuery(id+"F6.opExtrude","CAP_EDGE",EDGE,{"disambiguationData":[OSD([subQ1])],"isStart":false}),makeQuery(id+"F8.opExtrude","SWEPT_EDGE",EDGE,{"disambiguationData":[OSD([subQ1,subQ0]),TDD([makeQuery(id+"F6.opExtrude","CAP_VERTEX",VERTEX,{"disambiguationData":[OSD([subQ1,subQ0])],"isStart":false})])]})]}),makeQuery(id+"F8.opExtrude","CAP_FACE",FACE,{"disambiguationData":[OSD([subQ0])],"isStart":false})],"blendedInto":[makeQuery(id+"F8.opExtrude","CAP_FACE",FACE,{"disambiguationData":[OSD([subQ0])],"isStart":false})]});}
            var Q1;
            {var subQ0=sQuery(id+"F5.wireOp",EDGE,"E38");var subQ1=sQuery(id+"F5.wireOp",EDGE,"E33.0");Q1=makeQuery(id+"F20.opFillet","BLEND_EDGE",EDGE,{"blendedFrom":[makeQuery(id+"F7.boolean.opBoolean","MERGE",EDGE,{"derivedFrom":[makeQuery(id+"F6.opExtrude","CAP_EDGE",EDGE,{"disambiguationData":[OSD([subQ1])],"isStart":false}),makeQuery(id+"F7.opExtrude","SWEPT_EDGE",EDGE,{"disambiguationData":[OSD([subQ1,subQ0]),TDD([makeQuery(id+"F6.opExtrude","CAP_VERTEX",VERTEX,{"disambiguationData":[OSD([subQ1,subQ0])],"isStart":false})])]})]}),makeQuery(id+"F7.opExtrude","CAP_FACE",FACE,{"disambiguationData":[OSD([subQ0])],"isStart":false})],"blendedInto":[makeQuery(id+"F7.opExtrude","CAP_FACE",FACE,{"disambiguationData":[OSD([subQ0])],"isStart":false})]});}
            var Q2;
            {var subQ0=sQuery(id+"F5.wireOp",EDGE,"E35");var subQ1=sQuery(id+"F5.wireOp",EDGE,"E33.1");Q2=makeQuery(id+"F20.opFillet","BLEND_EDGE",EDGE,{"blendedFrom":[makeQuery(id+"F9.boolean.opBoolean","MERGE",EDGE,{"derivedFrom":[makeQuery(id+"F6.opExtrude","CAP_EDGE",EDGE,{"disambiguationData":[OSD([subQ1])],"isStart":false}),makeQuery(id+"F9.opExtrude","SWEPT_EDGE",EDGE,{"disambiguationData":[OSD([subQ1,subQ0]),TDD([makeQuery(id+"F6.opExtrude","CAP_VERTEX",VERTEX,{"disambiguationData":[OSD([subQ1,subQ0])],"isStart":false})])]})]}),makeQuery(id+"F9.opExtrude","CAP_FACE",FACE,{"disambiguationData":[OSD([subQ0])],"isStart":false})],"blendedInto":[makeQuery(id+"F9.opExtrude","CAP_FACE",FACE,{"disambiguationData":[OSD([subQ0])],"isStart":false})]});}
            var Q3;
            {var subQ0=sQuery(id+"F5.wireOp",EDGE,"E37");var subQ1=sQuery(id+"F5.wireOp",EDGE,"E32.1");Q3=makeQuery(id+"F20.opFillet","BLEND_EDGE",EDGE,{"blendedFrom":[makeQuery(id+"F10.boolean.opBoolean","MERGE",EDGE,{"derivedFrom":[makeQuery(id+"F6.opExtrude","CAP_EDGE",EDGE,{"disambiguationData":[OSD([subQ1])],"isStart":false}),makeQuery(id+"F10.opExtrude","SWEPT_EDGE",EDGE,{"disambiguationData":[OSD([subQ1,subQ0]),TDD([makeQuery(id+"F6.opExtrude","CAP_VERTEX",VERTEX,{"disambiguationData":[OSD([subQ1,subQ0])],"isStart":false})])]})]}),makeQuery(id+"F10.opExtrude","CAP_FACE",FACE,{"disambiguationData":[OSD([subQ0])],"isStart":false})],"blendedInto":[makeQuery(id+"F10.opExtrude","CAP_FACE",FACE,{"disambiguationData":[OSD([subQ0])],"isStart":false})]});}
            fillet(context, id + "F26", {"entities" : qUnion([Q0, Q1, Q2, Q3]), "radius" : 1 * mm, "tangentPropagation" : true, "allowEdgeOverflow" : false});
        }
        {
            var Q0;
            Q0=makeQuery(id+"F1.opExtrude","CAP_FACE",FACE,{"disambiguationData":[OSD([sQuery(id+"F0.wireOp",EDGE,"E1"),sQuery(id+"F0.wireOp",EDGE,"E2"),sQuery(id+"F0.wireOp",EDGE,"E3"),sQuery(id+"F0.wireOp",EDGE,"E4"),sQuery(id+"F0.wireOp",EDGE,"E5.bottom"),sQuery(id+"F0.wireOp",EDGE,"E5.top"),sQuery(id+"F0.wireOp",EDGE,"E5.left"),sQuery(id+"F0.wireOp",EDGE,"E5.right")])],"isStart":false});
            var sketch = newSketch(context, id + "F27", { "sketchPlane" : qUnion([Q0])});
            skLineSegment(sketch, "E55", {"start": v(-1.5, 19.25) * mm, "end": v(1.5, 19.25) * mm});
            skLineSegment(sketch, "E56", {"start": v(-19.25, 1.5) * mm, "end": v(-19.25, -1.5) * mm});
            skLineSegment(sketch, "E57", {"start": v(19.25, 1.5) * mm, "end": v(19.25, -1.5) * mm});
            skLineSegment(sketch, "E58", {"start": v(-1.5, -19.25) * mm, "end": v(1.5, -19.25) * mm});
            skCircle(sketch, "E59", {"center": v(-15.25, -15.25) * mm, "radius": 4 * mm});
            skCircle(sketch, "E60", {"center": v(-15.25, 15.25) * mm, "radius": 4 * mm});
            skCircle(sketch, "E61", {"center": v(15.25, 15.25) * mm, "radius": 4 * mm});
            skCircle(sketch, "E62", {"center": v(15.25, -15.25) * mm, "radius": 4 * mm});
            skSolve(sketch);
        }
        {
            var Q0;
            Q0=makeQuery(id+"F27.imprint","IMPRINT",FACE,{"disambiguationData":[TD([[makeQuery(id+"F27.imprint","IMPRINT",EDGE,{"derivedFrom":sQuery(id+"F27.wireOp",EDGE,"E55")}),-1.0]])]});
            extrude(context, id + "F28", {"entities" : qUnion([Q0]), "operationType" : NewBodyOperationType.REMOVE, "oppositeDirection" : true, "depth" : 1 * mm, "offsetDistance" : 25 * mm});
        }
    });
